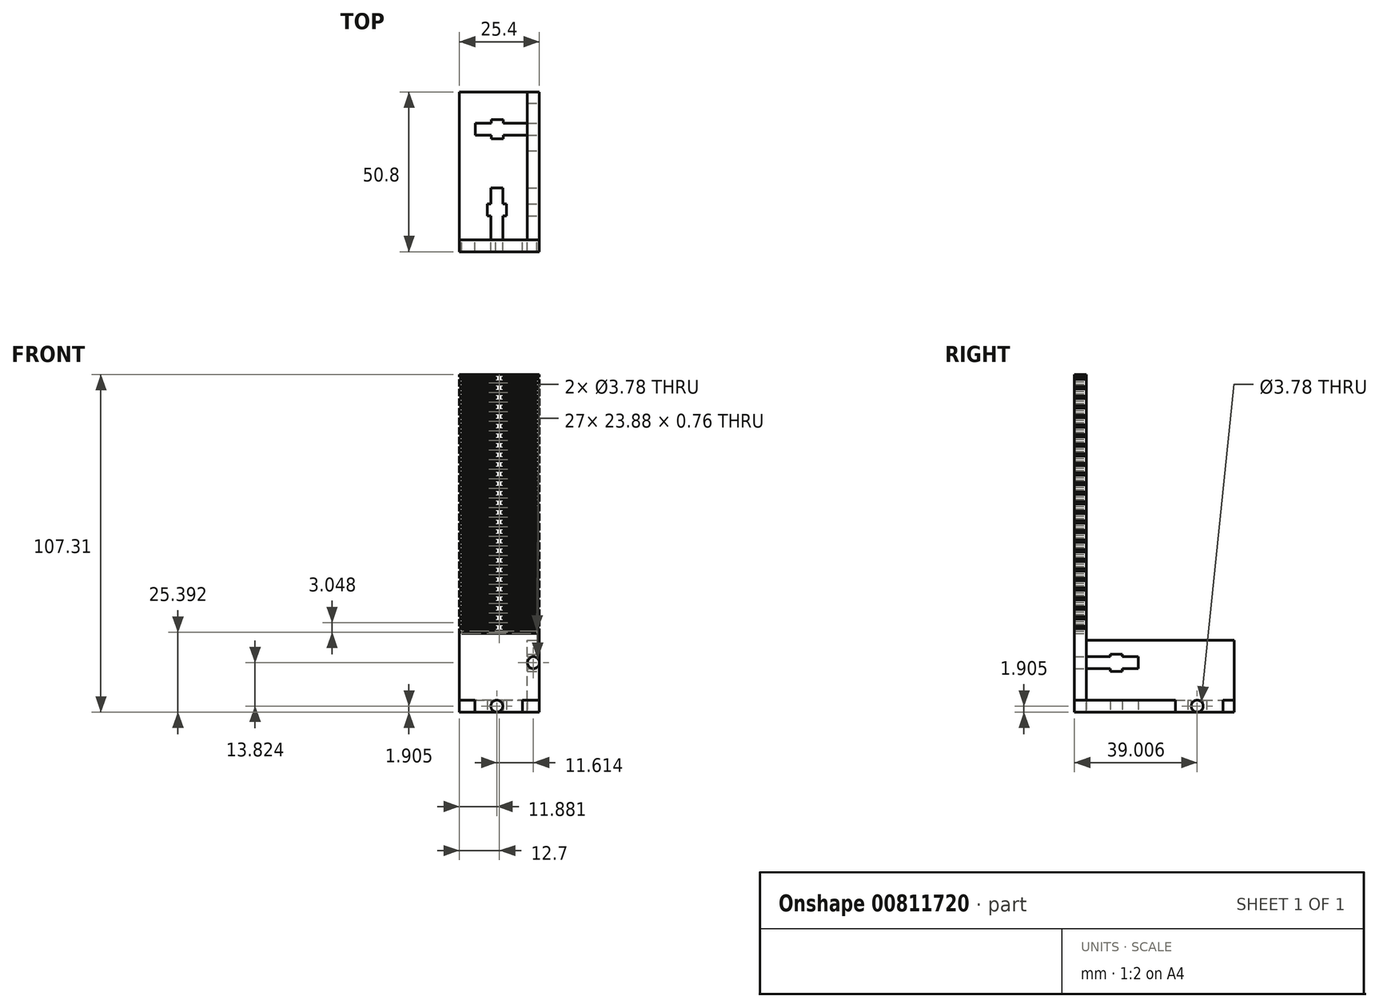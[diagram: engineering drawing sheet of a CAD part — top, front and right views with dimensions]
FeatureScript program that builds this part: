
annotation { "Feature Type Name" : "Feature", "Feature Type Description" : "" }
export const myFeature = defineFeature(function(context is Context, id is Id, definition is map)
    precondition{}
    {
        {
            var Q0;
            Q0=qCreatedBy(makeId("Top.planeOp"),FACE);
            var sketch = newSketch(context, id + "F0", { "sketchPlane" : qUnion([Q0])});
            skLineSegment(sketch, "E0.bottom", {"start": v(-25.4, -50.8) * mm, "end": v(-20.43, -50.8) * mm});
            skLineSegment(sketch, "E0.top", {"start": v(-25.4, 0) * mm, "end": v(0, 0) * mm});
            skLineSegment(sketch, "E0.left", {"start": v(-25.4, -50.8) * mm, "end": v(-25.4, 0) * mm});
            skLineSegment(sketch, "E0.right", {"start": v(0, -50.8) * mm, "end": v(0, -18.7) * mm});
            skLineSegment(sketch, "E1.bottom", {"start": v(-3.8, -9.89) * mm, "end": v(-11.43, -9.89) * mm});
            skLineSegment(sketch, "E1.top", {"start": v(-3.8, -13.7) * mm, "end": v(-11.43, -13.7) * mm});
            skLineSegment(sketch, "E1.right", {"start": v(-20.32, -9.89) * mm, "end": v(-20.32, -13.7) * mm});
            skLineSegment(sketch, "E2.bottom", {"start": v(-15.24, -14.83) * mm, "end": v(-11.43, -14.83) * mm});
            skLineSegment(sketch, "E2.top", {"start": v(-15.24, -8.76) * mm, "end": v(-11.43, -8.76) * mm});
            skLineSegment(sketch, "E2.left", {"start": v(-15.24, -14.83) * mm, "end": v(-15.24, -13.7) * mm});
            skLineSegment(sketch, "E2.right", {"start": v(-11.43, -14.83) * mm, "end": v(-11.43, -13.7) * mm});
            skLineSegment(sketch, "E3.trimOffspring", {"start": v(-11.43, -9.89) * mm, "end": v(-11.43, -8.76) * mm});
            skLineSegment(sketch, "E4.trimOffspring", {"start": v(-15.24, -9.89) * mm, "end": v(-15.24, -8.76) * mm});
            skLineSegment(sketch, "E5.trimOffspring", {"start": v(-15.24, -9.89) * mm, "end": v(-20.32, -9.89) * mm});
            skLineSegment(sketch, "E6.trimOffspring", {"start": v(-15.24, -13.7) * mm, "end": v(-20.32, -13.7) * mm});
            skLineSegment(sketch, "E7.bottom", {"start": v(0, -18.7) * mm, "end": v(-3.8, -18.7) * mm});
            skLineSegment(sketch, "E7.top", {"start": v(0, -3.62) * mm, "end": v(-3.8, -3.62) * mm});
            skLineSegment(sketch, "E7.right", {"start": v(-3.8, -18.7) * mm, "end": v(-3.8, -13.7) * mm});
            skLineSegment(sketch, "E8.trimOffspring", {"start": v(-3.8, -9.89) * mm, "end": v(-3.8, -3.62) * mm});
            skLineSegment(sketch, "E9.trimOffspring", {"start": v(0, -3.62) * mm, "end": v(0, 0) * mm});
            skLineSegment(sketch, "E10.bottom", {"start": v(-11.63, -46.99) * mm, "end": v(-11.63, -39.37) * mm});
            skLineSegment(sketch, "E10.top", {"start": v(-15.44, -46.99) * mm, "end": v(-15.44, -39.37) * mm});
            skLineSegment(sketch, "E10.right", {"start": v(-11.63, -30.48) * mm, "end": v(-15.44, -30.48) * mm});
            skLineSegment(sketch, "E11.bottom", {"start": v(-16.57, -35.56) * mm, "end": v(-16.57, -39.37) * mm});
            skLineSegment(sketch, "E11.top", {"start": v(-10.5, -35.56) * mm, "end": v(-10.5, -39.37) * mm});
            skLineSegment(sketch, "E11.left", {"start": v(-16.57, -35.56) * mm, "end": v(-15.44, -35.56) * mm});
            skLineSegment(sketch, "E11.right", {"start": v(-16.57, -39.37) * mm, "end": v(-15.44, -39.37) * mm});
            skLineSegment(sketch, "E12.trimOffspring", {"start": v(-11.63, -39.37) * mm, "end": v(-10.5, -39.37) * mm});
            skLineSegment(sketch, "E13.trimOffspring", {"start": v(-11.63, -35.56) * mm, "end": v(-10.5, -35.56) * mm});
            skLineSegment(sketch, "E14.trimOffspring", {"start": v(-11.63, -35.56) * mm, "end": v(-11.63, -30.48) * mm});
            skLineSegment(sketch, "E15.trimOffspring", {"start": v(-15.44, -35.56) * mm, "end": v(-15.44, -30.48) * mm});
            skLineSegment(sketch, "E16.bottom", {"start": v(-20.43, -50.8) * mm, "end": v(-20.43, -46.99) * mm});
            skLineSegment(sketch, "E16.top", {"start": v(-5.36, -50.8) * mm, "end": v(-5.36, -46.99) * mm});
            skLineSegment(sketch, "E16.right", {"start": v(-20.43, -46.99) * mm, "end": v(-15.44, -46.99) * mm});
            skLineSegment(sketch, "E17.trimOffspring", {"start": v(-11.63, -46.99) * mm, "end": v(-5.36, -46.99) * mm});
            skLineSegment(sketch, "E18.trimOffspring", {"start": v(-5.36, -50.8) * mm, "end": v(0, -50.8) * mm});
            skSolve(sketch);
        }
        {
            var Q0;
            Q0=makeQuery(id+"F0.imprint","IMPRINT",FACE,{"disambiguationData":[TD([[makeQuery(id+"F0.imprint","IMPRINT",EDGE,{"derivedFrom":sQuery(id+"F0.wireOp",EDGE,"E0.bottom")}),1.0]])]});
            extrude(context, id + "F1", {"entities" : qUnion([Q0]), "depth" : 3.8 * mm});
        }
        {
            var Q0;
            Q0=makeQuery(id+"F1.opExtrude","SWEPT_FACE",FACE,{"disambiguationData":[OSD([sQuery(id+"F0.wireOp",EDGE,"E16.right")])]});
            var sketch = newSketch(context, id + "F2", { "sketchPlane" : qUnion([Q0])});
            skLineSegment(sketch, "E19.bottom", {"start": v(-5.36, 0) * mm, "end": v(-20.43, 0) * mm});
            skLineSegment(sketch, "E20", {"start": v(-20.43, 0) * mm, "end": v(-20.43, 3.81) * mm});
            skLineSegment(sketch, "E21", {"start": v(-20.43, 3.81) * mm, "end": v(-25.4, 3.81) * mm});
            skLineSegment(sketch, "E22.MirrorCS", {"start": v(-5.36, 0) * mm, "end": v(-5.36, 3.81) * mm});
            skLineSegment(sketch, "E23.MirrorCS", {"start": v(-5.36, 3.81) * mm, "end": v(0, 3.81) * mm});
            skCircle(sketch, "E24", {"center": v(-13.52, 1.9) * mm, "radius": 1.9 * mm});
            skLineSegment(sketch, "E25", {"start": v(-20.43, 1.9) * mm, "end": v(-5.36, 1.9) * mm, "construction": true});
            skLineSegment(sketch, "E26", {"start": v(-25.4, 107.3) * mm, "end": v(-12.7, 107.3) * mm});
            skLineSegment(sketch, "E27", {"start": v(-12.7, 107.3) * mm, "end": v(-12.7, -12.92) * mm, "construction": true});
            skLineSegment(sketch, "E28.bottom", {"start": v(-25.4, 106.55) * mm, "end": v(-13.82, 106.55) * mm});
            skLineSegment(sketch, "E28.top", {"start": v(-25.4, 105.78) * mm, "end": v(-13.82, 105.78) * mm});
            skLineSegment(sketch, "E28.right", {"start": v(-13.82, 106.55) * mm, "end": v(-13.82, 105.78) * mm});
            skLineSegment(sketch, "E29.trimOffspring", {"start": v(-25.4, 106.55) * mm, "end": v(-25.4, 107.3) * mm});
            skPoint(sketch, "E30.start.orphan", {"position": v(0, 107.3) * mm});
            skLineSegment(sketch, "E31.MirrorCS", {"start": v(-11.58, 106.55) * mm, "end": v(-11.58, 105.78) * mm});
            skLineSegment(sketch, "E32.MirrorCS", {"start": v(0, 107.3) * mm, "end": v(-12.7, 107.3) * mm});
            skLineSegment(sketch, "E33.MirrorCS", {"start": v(0, 105.78) * mm, "end": v(-11.58, 105.78) * mm});
            skLineSegment(sketch, "E34.MirrorCS", {"start": v(0, 106.55) * mm, "end": v(0, 107.3) * mm});
            skLineSegment(sketch, "E35.MirrorCS", {"start": v(0, 106.55) * mm, "end": v(-11.58, 106.55) * mm});
            skLineSegment(sketch, "E36.bottom", {"start": v(-24.64, 105.02) * mm, "end": v(-0.76, 105.02) * mm});
            skLineSegment(sketch, "E36.top", {"start": v(-24.64, 104.26) * mm, "end": v(-0.76, 104.26) * mm});
            skLineSegment(sketch, "E36.left", {"start": v(-24.64, 105.02) * mm, "end": v(-24.64, 104.26) * mm});
            skLineSegment(sketch, "E36.right", {"start": v(-0.76, 105.02) * mm, "end": v(-0.76, 104.26) * mm});
            skLineSegment(sketch, "E37", {"start": v(-25.4, 105.78) * mm, "end": v(-25.4, 104.26) * mm});
            skLineSegment(sketch, "E38.MirrorCS", {"start": v(-38.1, 107.3) * mm, "end": v(-38.1, -12.92) * mm, "construction": true});
            skLineSegment(sketch, "E39.MirrorCS", {"start": v(0, 105.78) * mm, "end": v(0, 104.26) * mm});
            skLineSegment(sketch, "E40.0.1.0", {"start": v(-0.76, 101.97) * mm, "end": v(-0.76, 101.21) * mm});
            skLineSegment(sketch, "E40.0.1.1", {"start": v(0, 103.5) * mm, "end": v(0, 104.26) * mm});
            skPoint(sketch, "E40.0.1.2", {"position": v(0, 104.26) * mm});
            skLineSegment(sketch, "E40.0.1.3", {"start": v(-24.64, 101.97) * mm, "end": v(-24.64, 101.21) * mm});
            skLineSegment(sketch, "E40.0.1.4", {"start": v(0, 103.5) * mm, "end": v(-11.58, 103.5) * mm});
            skLineSegment(sketch, "E40.0.1.5", {"start": v(-25.4, 103.5) * mm, "end": v(-13.82, 103.5) * mm});
            skLineSegment(sketch, "E40.0.1.6", {"start": v(0, 102.74) * mm, "end": v(-11.58, 102.74) * mm});
            skLineSegment(sketch, "E40.0.1.7", {"start": v(0, 102.74) * mm, "end": v(0, 101.21) * mm});
            skLineSegment(sketch, "E40.0.1.8", {"start": v(-25.4, 102.74) * mm, "end": v(-25.4, 101.21) * mm});
            skLineSegment(sketch, "E40.0.1.9", {"start": v(-24.64, 101.21) * mm, "end": v(-0.76, 101.21) * mm});
            skLineSegment(sketch, "E40.0.1.10", {"start": v(-25.4, 103.5) * mm, "end": v(-25.4, 104.26) * mm});
            skLineSegment(sketch, "E40.0.1.11", {"start": v(-13.82, 103.5) * mm, "end": v(-13.82, 102.74) * mm});
            skLineSegment(sketch, "E40.0.1.12", {"start": v(-11.58, 103.5) * mm, "end": v(-11.58, 102.74) * mm});
            skLineSegment(sketch, "E40.0.1.13", {"start": v(-24.64, 101.97) * mm, "end": v(-0.76, 101.97) * mm});
            skLineSegment(sketch, "E40.0.1.14", {"start": v(-25.4, 102.74) * mm, "end": v(-13.82, 102.74) * mm});
            skLineSegment(sketch, "E40.0.2.0", {"start": v(-0.76, 98.93) * mm, "end": v(-0.76, 98.16) * mm});
            skLineSegment(sketch, "E40.0.2.1", {"start": v(0, 100.45) * mm, "end": v(0, 101.21) * mm});
            skPoint(sketch, "E40.0.2.2", {"position": v(0, 101.21) * mm});
            skLineSegment(sketch, "E40.0.2.3", {"start": v(-24.64, 98.93) * mm, "end": v(-24.64, 98.16) * mm});
            skLineSegment(sketch, "E40.0.2.4", {"start": v(0, 100.45) * mm, "end": v(-11.58, 100.45) * mm});
            skLineSegment(sketch, "E40.0.2.5", {"start": v(-25.4, 100.45) * mm, "end": v(-13.82, 100.45) * mm});
            skLineSegment(sketch, "E40.0.2.6", {"start": v(0, 99.69) * mm, "end": v(-11.58, 99.69) * mm});
            skLineSegment(sketch, "E40.0.2.7", {"start": v(0, 99.69) * mm, "end": v(0, 98.16) * mm});
            skLineSegment(sketch, "E40.0.2.8", {"start": v(-25.4, 99.69) * mm, "end": v(-25.4, 98.16) * mm});
            skLineSegment(sketch, "E40.0.2.9", {"start": v(-24.64, 98.16) * mm, "end": v(-0.76, 98.16) * mm});
            skLineSegment(sketch, "E40.0.2.10", {"start": v(-25.4, 100.45) * mm, "end": v(-25.4, 101.21) * mm});
            skLineSegment(sketch, "E40.0.2.11", {"start": v(-13.82, 100.45) * mm, "end": v(-13.82, 99.69) * mm});
            skLineSegment(sketch, "E40.0.2.12", {"start": v(-11.58, 100.45) * mm, "end": v(-11.58, 99.69) * mm});
            skLineSegment(sketch, "E40.0.2.13", {"start": v(-24.64, 98.93) * mm, "end": v(-0.76, 98.93) * mm});
            skLineSegment(sketch, "E40.0.2.14", {"start": v(-25.4, 99.69) * mm, "end": v(-13.82, 99.69) * mm});
            skLineSegment(sketch, "E40.0.3.0", {"start": v(-0.76, 95.88) * mm, "end": v(-0.76, 95.12) * mm});
            skLineSegment(sketch, "E40.0.3.1", {"start": v(0, 97.4) * mm, "end": v(0, 98.16) * mm});
            skPoint(sketch, "E40.0.3.2", {"position": v(0, 98.16) * mm});
            skLineSegment(sketch, "E40.0.3.3", {"start": v(-24.64, 95.88) * mm, "end": v(-24.64, 95.12) * mm});
            skLineSegment(sketch, "E40.0.3.4", {"start": v(0, 97.4) * mm, "end": v(-11.58, 97.4) * mm});
            skLineSegment(sketch, "E40.0.3.5", {"start": v(-25.4, 97.4) * mm, "end": v(-13.82, 97.4) * mm});
            skLineSegment(sketch, "E40.0.3.6", {"start": v(0, 96.64) * mm, "end": v(-11.58, 96.64) * mm});
            skLineSegment(sketch, "E40.0.3.7", {"start": v(0, 96.64) * mm, "end": v(0, 95.12) * mm});
            skLineSegment(sketch, "E40.0.3.8", {"start": v(-25.4, 96.64) * mm, "end": v(-25.4, 95.12) * mm});
            skLineSegment(sketch, "E40.0.3.9", {"start": v(-24.64, 95.12) * mm, "end": v(-0.76, 95.12) * mm});
            skLineSegment(sketch, "E40.0.3.10", {"start": v(-25.4, 97.4) * mm, "end": v(-25.4, 98.16) * mm});
            skLineSegment(sketch, "E40.0.3.11", {"start": v(-13.82, 97.4) * mm, "end": v(-13.82, 96.64) * mm});
            skLineSegment(sketch, "E40.0.3.12", {"start": v(-11.58, 97.4) * mm, "end": v(-11.58, 96.64) * mm});
            skLineSegment(sketch, "E40.0.3.13", {"start": v(-24.64, 95.88) * mm, "end": v(-0.76, 95.88) * mm});
            skLineSegment(sketch, "E40.0.3.14", {"start": v(-25.4, 96.64) * mm, "end": v(-13.82, 96.64) * mm});
            skLineSegment(sketch, "E40.0.4.0", {"start": v(-0.76, 92.83) * mm, "end": v(-0.76, 92.07) * mm});
            skLineSegment(sketch, "E40.0.4.1", {"start": v(0, 94.35) * mm, "end": v(0, 95.12) * mm});
            skPoint(sketch, "E40.0.4.2", {"position": v(0, 95.12) * mm});
            skLineSegment(sketch, "E40.0.4.3", {"start": v(-24.64, 92.83) * mm, "end": v(-24.64, 92.07) * mm});
            skLineSegment(sketch, "E40.0.4.4", {"start": v(0, 94.35) * mm, "end": v(-11.58, 94.35) * mm});
            skLineSegment(sketch, "E40.0.4.5", {"start": v(-25.4, 94.35) * mm, "end": v(-13.82, 94.35) * mm});
            skLineSegment(sketch, "E40.0.4.6", {"start": v(0, 93.6) * mm, "end": v(-11.58, 93.6) * mm});
            skLineSegment(sketch, "E40.0.4.7", {"start": v(0, 93.6) * mm, "end": v(0, 92.07) * mm});
            skLineSegment(sketch, "E40.0.4.8", {"start": v(-25.4, 93.6) * mm, "end": v(-25.4, 92.07) * mm});
            skLineSegment(sketch, "E40.0.4.9", {"start": v(-24.64, 92.07) * mm, "end": v(-0.76, 92.07) * mm});
            skLineSegment(sketch, "E40.0.4.10", {"start": v(-25.4, 94.35) * mm, "end": v(-25.4, 95.12) * mm});
            skLineSegment(sketch, "E40.0.4.11", {"start": v(-13.82, 94.35) * mm, "end": v(-13.82, 93.6) * mm});
            skLineSegment(sketch, "E40.0.4.12", {"start": v(-11.58, 94.35) * mm, "end": v(-11.58, 93.6) * mm});
            skLineSegment(sketch, "E40.0.4.13", {"start": v(-24.64, 92.83) * mm, "end": v(-0.76, 92.83) * mm});
            skLineSegment(sketch, "E40.0.4.14", {"start": v(-25.4, 93.6) * mm, "end": v(-13.82, 93.6) * mm});
            skLineSegment(sketch, "E40.0.5.0", {"start": v(-0.76, 89.78) * mm, "end": v(-0.76, 89.02) * mm});
            skLineSegment(sketch, "E40.0.5.1", {"start": v(0, 91.3) * mm, "end": v(0, 92.07) * mm});
            skPoint(sketch, "E40.0.5.2", {"position": v(0, 92.07) * mm});
            skLineSegment(sketch, "E40.0.5.3", {"start": v(-24.64, 89.78) * mm, "end": v(-24.64, 89.02) * mm});
            skLineSegment(sketch, "E40.0.5.4", {"start": v(0, 91.3) * mm, "end": v(-11.58, 91.3) * mm});
            skLineSegment(sketch, "E40.0.5.5", {"start": v(-25.4, 91.3) * mm, "end": v(-13.82, 91.3) * mm});
            skLineSegment(sketch, "E40.0.5.6", {"start": v(0, 90.54) * mm, "end": v(-11.58, 90.54) * mm});
            skLineSegment(sketch, "E40.0.5.7", {"start": v(0, 90.54) * mm, "end": v(0, 89.02) * mm});
            skLineSegment(sketch, "E40.0.5.8", {"start": v(-25.4, 90.54) * mm, "end": v(-25.4, 89.02) * mm});
            skLineSegment(sketch, "E40.0.5.9", {"start": v(-24.64, 89.02) * mm, "end": v(-0.76, 89.02) * mm});
            skLineSegment(sketch, "E40.0.5.10", {"start": v(-25.4, 91.3) * mm, "end": v(-25.4, 92.07) * mm});
            skLineSegment(sketch, "E40.0.5.11", {"start": v(-13.82, 91.3) * mm, "end": v(-13.82, 90.54) * mm});
            skLineSegment(sketch, "E40.0.5.12", {"start": v(-11.58, 91.3) * mm, "end": v(-11.58, 90.54) * mm});
            skLineSegment(sketch, "E40.0.5.13", {"start": v(-24.64, 89.78) * mm, "end": v(-0.76, 89.78) * mm});
            skLineSegment(sketch, "E40.0.5.14", {"start": v(-25.4, 90.54) * mm, "end": v(-13.82, 90.54) * mm});
            skLineSegment(sketch, "E40.0.6.0", {"start": v(-0.76, 86.73) * mm, "end": v(-0.76, 85.97) * mm});
            skLineSegment(sketch, "E40.0.6.1", {"start": v(0, 88.26) * mm, "end": v(0, 89.02) * mm});
            skPoint(sketch, "E40.0.6.2", {"position": v(0, 89.02) * mm});
            skLineSegment(sketch, "E40.0.6.3", {"start": v(-24.64, 86.73) * mm, "end": v(-24.64, 85.97) * mm});
            skLineSegment(sketch, "E40.0.6.4", {"start": v(0, 88.26) * mm, "end": v(-11.58, 88.26) * mm});
            skLineSegment(sketch, "E40.0.6.5", {"start": v(-25.4, 88.26) * mm, "end": v(-13.82, 88.26) * mm});
            skLineSegment(sketch, "E40.0.6.6", {"start": v(0, 87.5) * mm, "end": v(-11.58, 87.5) * mm});
            skLineSegment(sketch, "E40.0.6.7", {"start": v(0, 87.5) * mm, "end": v(0, 85.97) * mm});
            skLineSegment(sketch, "E40.0.6.8", {"start": v(-25.4, 87.5) * mm, "end": v(-25.4, 85.97) * mm});
            skLineSegment(sketch, "E40.0.6.9", {"start": v(-24.64, 85.97) * mm, "end": v(-0.76, 85.97) * mm});
            skLineSegment(sketch, "E40.0.6.10", {"start": v(-25.4, 88.26) * mm, "end": v(-25.4, 89.02) * mm});
            skLineSegment(sketch, "E40.0.6.11", {"start": v(-13.82, 88.26) * mm, "end": v(-13.82, 87.5) * mm});
            skLineSegment(sketch, "E40.0.6.12", {"start": v(-11.58, 88.26) * mm, "end": v(-11.58, 87.5) * mm});
            skLineSegment(sketch, "E40.0.6.13", {"start": v(-24.64, 86.73) * mm, "end": v(-0.76, 86.73) * mm});
            skLineSegment(sketch, "E40.0.6.14", {"start": v(-25.4, 87.5) * mm, "end": v(-13.82, 87.5) * mm});
            skLineSegment(sketch, "E40.0.7.0", {"start": v(-0.76, 83.69) * mm, "end": v(-0.76, 82.92) * mm});
            skLineSegment(sketch, "E40.0.7.1", {"start": v(0, 85.2) * mm, "end": v(0, 85.97) * mm});
            skPoint(sketch, "E40.0.7.2", {"position": v(0, 85.97) * mm});
            skLineSegment(sketch, "E40.0.7.3", {"start": v(-24.64, 83.69) * mm, "end": v(-24.64, 82.92) * mm});
            skLineSegment(sketch, "E40.0.7.4", {"start": v(0, 85.2) * mm, "end": v(-11.58, 85.2) * mm});
            skLineSegment(sketch, "E40.0.7.5", {"start": v(-25.4, 85.2) * mm, "end": v(-13.82, 85.2) * mm});
            skLineSegment(sketch, "E40.0.7.6", {"start": v(0, 84.45) * mm, "end": v(-11.58, 84.45) * mm});
            skLineSegment(sketch, "E40.0.7.7", {"start": v(0, 84.45) * mm, "end": v(0, 82.92) * mm});
            skLineSegment(sketch, "E40.0.7.8", {"start": v(-25.4, 84.45) * mm, "end": v(-25.4, 82.92) * mm});
            skLineSegment(sketch, "E40.0.7.9", {"start": v(-24.64, 82.92) * mm, "end": v(-0.76, 82.92) * mm});
            skLineSegment(sketch, "E40.0.7.10", {"start": v(-25.4, 85.2) * mm, "end": v(-25.4, 85.97) * mm});
            skLineSegment(sketch, "E40.0.7.11", {"start": v(-13.82, 85.2) * mm, "end": v(-13.82, 84.45) * mm});
            skLineSegment(sketch, "E40.0.7.12", {"start": v(-11.58, 85.2) * mm, "end": v(-11.58, 84.45) * mm});
            skLineSegment(sketch, "E40.0.7.13", {"start": v(-24.64, 83.69) * mm, "end": v(-0.76, 83.69) * mm});
            skLineSegment(sketch, "E40.0.7.14", {"start": v(-25.4, 84.45) * mm, "end": v(-13.82, 84.45) * mm});
            skLineSegment(sketch, "E40.0.8.0", {"start": v(-0.76, 80.64) * mm, "end": v(-0.76, 79.88) * mm});
            skLineSegment(sketch, "E40.0.8.1", {"start": v(0, 82.16) * mm, "end": v(0, 82.92) * mm});
            skPoint(sketch, "E40.0.8.2", {"position": v(0, 82.92) * mm});
            skLineSegment(sketch, "E40.0.8.3", {"start": v(-24.64, 80.64) * mm, "end": v(-24.64, 79.88) * mm});
            skLineSegment(sketch, "E40.0.8.4", {"start": v(0, 82.16) * mm, "end": v(-11.58, 82.16) * mm});
            skLineSegment(sketch, "E40.0.8.5", {"start": v(-25.4, 82.16) * mm, "end": v(-13.82, 82.16) * mm});
            skLineSegment(sketch, "E40.0.8.6", {"start": v(0, 81.4) * mm, "end": v(-11.58, 81.4) * mm});
            skLineSegment(sketch, "E40.0.8.7", {"start": v(0, 81.4) * mm, "end": v(0, 79.88) * mm});
            skLineSegment(sketch, "E40.0.8.8", {"start": v(-25.4, 81.4) * mm, "end": v(-25.4, 79.88) * mm});
            skLineSegment(sketch, "E40.0.8.9", {"start": v(-24.64, 79.88) * mm, "end": v(-0.76, 79.88) * mm});
            skLineSegment(sketch, "E40.0.8.10", {"start": v(-25.4, 82.16) * mm, "end": v(-25.4, 82.92) * mm});
            skLineSegment(sketch, "E40.0.8.11", {"start": v(-13.82, 82.16) * mm, "end": v(-13.82, 81.4) * mm});
            skLineSegment(sketch, "E40.0.8.12", {"start": v(-11.58, 82.16) * mm, "end": v(-11.58, 81.4) * mm});
            skLineSegment(sketch, "E40.0.8.13", {"start": v(-24.64, 80.64) * mm, "end": v(-0.76, 80.64) * mm});
            skLineSegment(sketch, "E40.0.8.14", {"start": v(-25.4, 81.4) * mm, "end": v(-13.82, 81.4) * mm});
            skLineSegment(sketch, "E40.0.9.0", {"start": v(-0.76, 77.59) * mm, "end": v(-0.76, 76.83) * mm});
            skLineSegment(sketch, "E40.0.9.1", {"start": v(0, 79.11) * mm, "end": v(0, 79.88) * mm});
            skPoint(sketch, "E40.0.9.2", {"position": v(0, 79.88) * mm});
            skLineSegment(sketch, "E40.0.9.3", {"start": v(-24.64, 77.59) * mm, "end": v(-24.64, 76.83) * mm});
            skLineSegment(sketch, "E40.0.9.4", {"start": v(0, 79.11) * mm, "end": v(-11.58, 79.11) * mm});
            skLineSegment(sketch, "E40.0.9.5", {"start": v(-25.4, 79.11) * mm, "end": v(-13.82, 79.11) * mm});
            skLineSegment(sketch, "E40.0.9.6", {"start": v(0, 78.35) * mm, "end": v(-11.58, 78.35) * mm});
            skLineSegment(sketch, "E40.0.9.7", {"start": v(0, 78.35) * mm, "end": v(0, 76.83) * mm});
            skLineSegment(sketch, "E40.0.9.8", {"start": v(-25.4, 78.35) * mm, "end": v(-25.4, 76.83) * mm});
            skLineSegment(sketch, "E40.0.9.9", {"start": v(-24.64, 76.83) * mm, "end": v(-0.76, 76.83) * mm});
            skLineSegment(sketch, "E40.0.9.10", {"start": v(-25.4, 79.11) * mm, "end": v(-25.4, 79.88) * mm});
            skLineSegment(sketch, "E40.0.9.11", {"start": v(-13.82, 79.11) * mm, "end": v(-13.82, 78.35) * mm});
            skLineSegment(sketch, "E40.0.9.12", {"start": v(-11.58, 79.11) * mm, "end": v(-11.58, 78.35) * mm});
            skLineSegment(sketch, "E40.0.9.13", {"start": v(-24.64, 77.59) * mm, "end": v(-0.76, 77.59) * mm});
            skLineSegment(sketch, "E40.0.9.14", {"start": v(-25.4, 78.35) * mm, "end": v(-13.82, 78.35) * mm});
            skLineSegment(sketch, "E40.0.10.0", {"start": v(-0.76, 74.54) * mm, "end": v(-0.76, 73.78) * mm});
            skLineSegment(sketch, "E40.0.10.1", {"start": v(0, 76.07) * mm, "end": v(0, 76.83) * mm});
            skPoint(sketch, "E40.0.10.2", {"position": v(0, 76.83) * mm});
            skLineSegment(sketch, "E40.0.10.3", {"start": v(-24.64, 74.54) * mm, "end": v(-24.64, 73.78) * mm});
            skLineSegment(sketch, "E40.0.10.4", {"start": v(0, 76.07) * mm, "end": v(-11.58, 76.07) * mm});
            skLineSegment(sketch, "E40.0.10.5", {"start": v(-25.4, 76.07) * mm, "end": v(-13.82, 76.07) * mm});
            skLineSegment(sketch, "E40.0.10.6", {"start": v(0, 75.3) * mm, "end": v(-11.58, 75.3) * mm});
            skLineSegment(sketch, "E40.0.10.7", {"start": v(0, 75.3) * mm, "end": v(0, 73.78) * mm});
            skLineSegment(sketch, "E40.0.10.8", {"start": v(-25.4, 75.3) * mm, "end": v(-25.4, 73.78) * mm});
            skLineSegment(sketch, "E40.0.10.9", {"start": v(-24.64, 73.78) * mm, "end": v(-0.76, 73.78) * mm});
            skLineSegment(sketch, "E40.0.10.10", {"start": v(-25.4, 76.07) * mm, "end": v(-25.4, 76.83) * mm});
            skLineSegment(sketch, "E40.0.10.11", {"start": v(-13.82, 76.07) * mm, "end": v(-13.82, 75.3) * mm});
            skLineSegment(sketch, "E40.0.10.12", {"start": v(-11.58, 76.07) * mm, "end": v(-11.58, 75.3) * mm});
            skLineSegment(sketch, "E40.0.10.13", {"start": v(-24.64, 74.54) * mm, "end": v(-0.76, 74.54) * mm});
            skLineSegment(sketch, "E40.0.10.14", {"start": v(-25.4, 75.3) * mm, "end": v(-13.82, 75.3) * mm});
            skLineSegment(sketch, "E40.0.11.0", {"start": v(-0.76, 71.5) * mm, "end": v(-0.76, 70.73) * mm});
            skLineSegment(sketch, "E40.0.11.1", {"start": v(0, 73.02) * mm, "end": v(0, 73.78) * mm});
            skPoint(sketch, "E40.0.11.2", {"position": v(0, 73.78) * mm});
            skLineSegment(sketch, "E40.0.11.3", {"start": v(-24.64, 71.5) * mm, "end": v(-24.64, 70.73) * mm});
            skLineSegment(sketch, "E40.0.11.4", {"start": v(0, 73.02) * mm, "end": v(-11.58, 73.02) * mm});
            skLineSegment(sketch, "E40.0.11.5", {"start": v(-25.4, 73.02) * mm, "end": v(-13.82, 73.02) * mm});
            skLineSegment(sketch, "E40.0.11.6", {"start": v(0, 72.26) * mm, "end": v(-11.58, 72.26) * mm});
            skLineSegment(sketch, "E40.0.11.7", {"start": v(0, 72.26) * mm, "end": v(0, 70.73) * mm});
            skLineSegment(sketch, "E40.0.11.8", {"start": v(-25.4, 72.26) * mm, "end": v(-25.4, 70.73) * mm});
            skLineSegment(sketch, "E40.0.11.9", {"start": v(-24.64, 70.73) * mm, "end": v(-0.76, 70.73) * mm});
            skLineSegment(sketch, "E40.0.11.10", {"start": v(-25.4, 73.02) * mm, "end": v(-25.4, 73.78) * mm});
            skLineSegment(sketch, "E40.0.11.11", {"start": v(-13.82, 73.02) * mm, "end": v(-13.82, 72.26) * mm});
            skLineSegment(sketch, "E40.0.11.12", {"start": v(-11.58, 73.02) * mm, "end": v(-11.58, 72.26) * mm});
            skLineSegment(sketch, "E40.0.11.13", {"start": v(-24.64, 71.5) * mm, "end": v(-0.76, 71.5) * mm});
            skLineSegment(sketch, "E40.0.11.14", {"start": v(-25.4, 72.26) * mm, "end": v(-13.82, 72.26) * mm});
            skLineSegment(sketch, "E40.0.12.0", {"start": v(-0.76, 68.45) * mm, "end": v(-0.76, 67.68) * mm});
            skLineSegment(sketch, "E40.0.12.1", {"start": v(0, 69.97) * mm, "end": v(0, 70.73) * mm});
            skPoint(sketch, "E40.0.12.2", {"position": v(0, 70.73) * mm});
            skLineSegment(sketch, "E40.0.12.3", {"start": v(-24.64, 68.45) * mm, "end": v(-24.64, 67.68) * mm});
            skLineSegment(sketch, "E40.0.12.4", {"start": v(0, 69.97) * mm, "end": v(-11.58, 69.97) * mm});
            skLineSegment(sketch, "E40.0.12.5", {"start": v(-25.4, 69.97) * mm, "end": v(-13.82, 69.97) * mm});
            skLineSegment(sketch, "E40.0.12.6", {"start": v(0, 69.2) * mm, "end": v(-11.58, 69.2) * mm});
            skLineSegment(sketch, "E40.0.12.7", {"start": v(0, 69.2) * mm, "end": v(0, 67.68) * mm});
            skLineSegment(sketch, "E40.0.12.8", {"start": v(-25.4, 69.2) * mm, "end": v(-25.4, 67.68) * mm});
            skLineSegment(sketch, "E40.0.12.9", {"start": v(-24.64, 67.68) * mm, "end": v(-0.76, 67.68) * mm});
            skLineSegment(sketch, "E40.0.12.10", {"start": v(-25.4, 69.97) * mm, "end": v(-25.4, 70.73) * mm});
            skLineSegment(sketch, "E40.0.12.11", {"start": v(-13.82, 69.97) * mm, "end": v(-13.82, 69.2) * mm});
            skLineSegment(sketch, "E40.0.12.12", {"start": v(-11.58, 69.97) * mm, "end": v(-11.58, 69.2) * mm});
            skLineSegment(sketch, "E40.0.12.13", {"start": v(-24.64, 68.45) * mm, "end": v(-0.76, 68.45) * mm});
            skLineSegment(sketch, "E40.0.12.14", {"start": v(-25.4, 69.2) * mm, "end": v(-13.82, 69.2) * mm});
            skLineSegment(sketch, "E40.0.13.0", {"start": v(-0.76, 65.4) * mm, "end": v(-0.76, 64.64) * mm});
            skLineSegment(sketch, "E40.0.13.1", {"start": v(0, 66.92) * mm, "end": v(0, 67.68) * mm});
            skPoint(sketch, "E40.0.13.2", {"position": v(0, 67.68) * mm});
            skLineSegment(sketch, "E40.0.13.3", {"start": v(-24.64, 65.4) * mm, "end": v(-24.64, 64.64) * mm});
            skLineSegment(sketch, "E40.0.13.4", {"start": v(0, 66.92) * mm, "end": v(-11.58, 66.92) * mm});
            skLineSegment(sketch, "E40.0.13.5", {"start": v(-25.4, 66.92) * mm, "end": v(-13.82, 66.92) * mm});
            skLineSegment(sketch, "E40.0.13.6", {"start": v(0, 66.16) * mm, "end": v(-11.58, 66.16) * mm});
            skLineSegment(sketch, "E40.0.13.7", {"start": v(0, 66.16) * mm, "end": v(0, 64.64) * mm});
            skLineSegment(sketch, "E40.0.13.8", {"start": v(-25.4, 66.16) * mm, "end": v(-25.4, 64.64) * mm});
            skLineSegment(sketch, "E40.0.13.9", {"start": v(-24.64, 64.64) * mm, "end": v(-0.76, 64.64) * mm});
            skLineSegment(sketch, "E40.0.13.10", {"start": v(-25.4, 66.92) * mm, "end": v(-25.4, 67.68) * mm});
            skLineSegment(sketch, "E40.0.13.11", {"start": v(-13.82, 66.92) * mm, "end": v(-13.82, 66.16) * mm});
            skLineSegment(sketch, "E40.0.13.12", {"start": v(-11.58, 66.92) * mm, "end": v(-11.58, 66.16) * mm});
            skLineSegment(sketch, "E40.0.13.13", {"start": v(-24.64, 65.4) * mm, "end": v(-0.76, 65.4) * mm});
            skLineSegment(sketch, "E40.0.13.14", {"start": v(-25.4, 66.16) * mm, "end": v(-13.82, 66.16) * mm});
            skLineSegment(sketch, "E40.0.14.0", {"start": v(-0.76, 62.35) * mm, "end": v(-0.76, 61.59) * mm});
            skLineSegment(sketch, "E40.0.14.1", {"start": v(0, 63.87) * mm, "end": v(0, 64.64) * mm});
            skPoint(sketch, "E40.0.14.2", {"position": v(0, 64.64) * mm});
            skLineSegment(sketch, "E40.0.14.3", {"start": v(-24.64, 62.35) * mm, "end": v(-24.64, 61.59) * mm});
            skLineSegment(sketch, "E40.0.14.4", {"start": v(0, 63.87) * mm, "end": v(-11.58, 63.87) * mm});
            skLineSegment(sketch, "E40.0.14.5", {"start": v(-25.4, 63.87) * mm, "end": v(-13.82, 63.87) * mm});
            skLineSegment(sketch, "E40.0.14.6", {"start": v(0, 63.11) * mm, "end": v(-11.58, 63.11) * mm});
            skLineSegment(sketch, "E40.0.14.7", {"start": v(0, 63.11) * mm, "end": v(0, 61.59) * mm});
            skLineSegment(sketch, "E40.0.14.8", {"start": v(-25.4, 63.11) * mm, "end": v(-25.4, 61.59) * mm});
            skLineSegment(sketch, "E40.0.14.9", {"start": v(-24.64, 61.59) * mm, "end": v(-0.76, 61.59) * mm});
            skLineSegment(sketch, "E40.0.14.10", {"start": v(-25.4, 63.87) * mm, "end": v(-25.4, 64.64) * mm});
            skLineSegment(sketch, "E40.0.14.11", {"start": v(-13.82, 63.87) * mm, "end": v(-13.82, 63.11) * mm});
            skLineSegment(sketch, "E40.0.14.12", {"start": v(-11.58, 63.87) * mm, "end": v(-11.58, 63.11) * mm});
            skLineSegment(sketch, "E40.0.14.13", {"start": v(-24.64, 62.35) * mm, "end": v(-0.76, 62.35) * mm});
            skLineSegment(sketch, "E40.0.14.14", {"start": v(-25.4, 63.11) * mm, "end": v(-13.82, 63.11) * mm});
            skLineSegment(sketch, "E40.0.15.0", {"start": v(-0.76, 59.3) * mm, "end": v(-0.76, 58.54) * mm});
            skLineSegment(sketch, "E40.0.15.1", {"start": v(0, 60.83) * mm, "end": v(0, 61.59) * mm});
            skPoint(sketch, "E40.0.15.2", {"position": v(0, 61.59) * mm});
            skLineSegment(sketch, "E40.0.15.3", {"start": v(-24.64, 59.3) * mm, "end": v(-24.64, 58.54) * mm});
            skLineSegment(sketch, "E40.0.15.4", {"start": v(0, 60.83) * mm, "end": v(-11.58, 60.83) * mm});
            skLineSegment(sketch, "E40.0.15.5", {"start": v(-25.4, 60.83) * mm, "end": v(-13.82, 60.83) * mm});
            skLineSegment(sketch, "E40.0.15.6", {"start": v(0, 60.06) * mm, "end": v(-11.58, 60.06) * mm});
            skLineSegment(sketch, "E40.0.15.7", {"start": v(0, 60.06) * mm, "end": v(0, 58.54) * mm});
            skLineSegment(sketch, "E40.0.15.8", {"start": v(-25.4, 60.06) * mm, "end": v(-25.4, 58.54) * mm});
            skLineSegment(sketch, "E40.0.15.9", {"start": v(-24.64, 58.54) * mm, "end": v(-0.76, 58.54) * mm});
            skLineSegment(sketch, "E40.0.15.10", {"start": v(-25.4, 60.83) * mm, "end": v(-25.4, 61.59) * mm});
            skLineSegment(sketch, "E40.0.15.11", {"start": v(-13.82, 60.83) * mm, "end": v(-13.82, 60.06) * mm});
            skLineSegment(sketch, "E40.0.15.12", {"start": v(-11.58, 60.83) * mm, "end": v(-11.58, 60.06) * mm});
            skLineSegment(sketch, "E40.0.15.13", {"start": v(-24.64, 59.3) * mm, "end": v(-0.76, 59.3) * mm});
            skLineSegment(sketch, "E40.0.15.14", {"start": v(-25.4, 60.06) * mm, "end": v(-13.82, 60.06) * mm});
            skLineSegment(sketch, "E40.0.16.0", {"start": v(-0.76, 56.25) * mm, "end": v(-0.76, 55.5) * mm});
            skLineSegment(sketch, "E40.0.16.1", {"start": v(0, 57.78) * mm, "end": v(0, 58.54) * mm});
            skPoint(sketch, "E40.0.16.2", {"position": v(0, 58.54) * mm});
            skLineSegment(sketch, "E40.0.16.3", {"start": v(-24.64, 56.25) * mm, "end": v(-24.64, 55.5) * mm});
            skLineSegment(sketch, "E40.0.16.4", {"start": v(0, 57.78) * mm, "end": v(-11.58, 57.78) * mm});
            skLineSegment(sketch, "E40.0.16.5", {"start": v(-25.4, 57.78) * mm, "end": v(-13.82, 57.78) * mm});
            skLineSegment(sketch, "E40.0.16.6", {"start": v(0, 57.02) * mm, "end": v(-11.58, 57.02) * mm});
            skLineSegment(sketch, "E40.0.16.7", {"start": v(0, 57.02) * mm, "end": v(0, 55.5) * mm});
            skLineSegment(sketch, "E40.0.16.8", {"start": v(-25.4, 57.02) * mm, "end": v(-25.4, 55.5) * mm});
            skLineSegment(sketch, "E40.0.16.9", {"start": v(-24.64, 55.5) * mm, "end": v(-0.76, 55.5) * mm});
            skLineSegment(sketch, "E40.0.16.10", {"start": v(-25.4, 57.78) * mm, "end": v(-25.4, 58.54) * mm});
            skLineSegment(sketch, "E40.0.16.11", {"start": v(-13.82, 57.78) * mm, "end": v(-13.82, 57.02) * mm});
            skLineSegment(sketch, "E40.0.16.12", {"start": v(-11.58, 57.78) * mm, "end": v(-11.58, 57.02) * mm});
            skLineSegment(sketch, "E40.0.16.13", {"start": v(-24.64, 56.25) * mm, "end": v(-0.76, 56.25) * mm});
            skLineSegment(sketch, "E40.0.16.14", {"start": v(-25.4, 57.02) * mm, "end": v(-13.82, 57.02) * mm});
            skLineSegment(sketch, "E40.0.17.0", {"start": v(-0.76, 53.2) * mm, "end": v(-0.76, 52.44) * mm});
            skLineSegment(sketch, "E40.0.17.1", {"start": v(0, 54.73) * mm, "end": v(0, 55.5) * mm});
            skPoint(sketch, "E40.0.17.2", {"position": v(0, 55.5) * mm});
            skLineSegment(sketch, "E40.0.17.3", {"start": v(-24.64, 53.2) * mm, "end": v(-24.64, 52.44) * mm});
            skLineSegment(sketch, "E40.0.17.4", {"start": v(0, 54.73) * mm, "end": v(-11.58, 54.73) * mm});
            skLineSegment(sketch, "E40.0.17.5", {"start": v(-25.4, 54.73) * mm, "end": v(-13.82, 54.73) * mm});
            skLineSegment(sketch, "E40.0.17.6", {"start": v(0, 53.97) * mm, "end": v(-11.58, 53.97) * mm});
            skLineSegment(sketch, "E40.0.17.7", {"start": v(0, 53.97) * mm, "end": v(0, 52.44) * mm});
            skLineSegment(sketch, "E40.0.17.8", {"start": v(-25.4, 53.97) * mm, "end": v(-25.4, 52.44) * mm});
            skLineSegment(sketch, "E40.0.17.9", {"start": v(-24.64, 52.44) * mm, "end": v(-0.76, 52.44) * mm});
            skLineSegment(sketch, "E40.0.17.10", {"start": v(-25.4, 54.73) * mm, "end": v(-25.4, 55.5) * mm});
            skLineSegment(sketch, "E40.0.17.11", {"start": v(-13.82, 54.73) * mm, "end": v(-13.82, 53.97) * mm});
            skLineSegment(sketch, "E40.0.17.12", {"start": v(-11.58, 54.73) * mm, "end": v(-11.58, 53.97) * mm});
            skLineSegment(sketch, "E40.0.17.13", {"start": v(-24.64, 53.2) * mm, "end": v(-0.76, 53.2) * mm});
            skLineSegment(sketch, "E40.0.17.14", {"start": v(-25.4, 53.97) * mm, "end": v(-13.82, 53.97) * mm});
            skLineSegment(sketch, "E40.0.18.0", {"start": v(-0.76, 50.16) * mm, "end": v(-0.76, 49.4) * mm});
            skLineSegment(sketch, "E40.0.18.1", {"start": v(0, 51.68) * mm, "end": v(0, 52.44) * mm});
            skPoint(sketch, "E40.0.18.2", {"position": v(0, 52.44) * mm});
            skLineSegment(sketch, "E40.0.18.3", {"start": v(-24.64, 50.16) * mm, "end": v(-24.64, 49.4) * mm});
            skLineSegment(sketch, "E40.0.18.4", {"start": v(0, 51.68) * mm, "end": v(-11.58, 51.68) * mm});
            skLineSegment(sketch, "E40.0.18.5", {"start": v(-25.4, 51.68) * mm, "end": v(-13.82, 51.68) * mm});
            skLineSegment(sketch, "E40.0.18.6", {"start": v(0, 50.92) * mm, "end": v(-11.58, 50.92) * mm});
            skLineSegment(sketch, "E40.0.18.7", {"start": v(0, 50.92) * mm, "end": v(0, 49.4) * mm});
            skLineSegment(sketch, "E40.0.18.8", {"start": v(-25.4, 50.92) * mm, "end": v(-25.4, 49.4) * mm});
            skLineSegment(sketch, "E40.0.18.9", {"start": v(-24.64, 49.4) * mm, "end": v(-0.76, 49.4) * mm});
            skLineSegment(sketch, "E40.0.18.10", {"start": v(-25.4, 51.68) * mm, "end": v(-25.4, 52.44) * mm});
            skLineSegment(sketch, "E40.0.18.11", {"start": v(-13.82, 51.68) * mm, "end": v(-13.82, 50.92) * mm});
            skLineSegment(sketch, "E40.0.18.12", {"start": v(-11.58, 51.68) * mm, "end": v(-11.58, 50.92) * mm});
            skLineSegment(sketch, "E40.0.18.13", {"start": v(-24.64, 50.16) * mm, "end": v(-0.76, 50.16) * mm});
            skLineSegment(sketch, "E40.0.18.14", {"start": v(-25.4, 50.92) * mm, "end": v(-13.82, 50.92) * mm});
            skLineSegment(sketch, "E40.0.19.0", {"start": v(-0.76, 47.1) * mm, "end": v(-0.76, 46.35) * mm});
            skLineSegment(sketch, "E40.0.19.1", {"start": v(0, 48.63) * mm, "end": v(0, 49.4) * mm});
            skPoint(sketch, "E40.0.19.2", {"position": v(0, 49.4) * mm});
            skLineSegment(sketch, "E40.0.19.3", {"start": v(-24.64, 47.1) * mm, "end": v(-24.64, 46.35) * mm});
            skLineSegment(sketch, "E40.0.19.4", {"start": v(0, 48.63) * mm, "end": v(-11.58, 48.63) * mm});
            skLineSegment(sketch, "E40.0.19.5", {"start": v(-25.4, 48.63) * mm, "end": v(-13.82, 48.63) * mm});
            skLineSegment(sketch, "E40.0.19.6", {"start": v(0, 47.87) * mm, "end": v(-11.58, 47.87) * mm});
            skLineSegment(sketch, "E40.0.19.7", {"start": v(0, 47.87) * mm, "end": v(0, 46.35) * mm});
            skLineSegment(sketch, "E40.0.19.8", {"start": v(-25.4, 47.87) * mm, "end": v(-25.4, 46.35) * mm});
            skLineSegment(sketch, "E40.0.19.9", {"start": v(-24.64, 46.35) * mm, "end": v(-0.76, 46.35) * mm});
            skLineSegment(sketch, "E40.0.19.10", {"start": v(-25.4, 48.63) * mm, "end": v(-25.4, 49.4) * mm});
            skLineSegment(sketch, "E40.0.19.11", {"start": v(-13.82, 48.63) * mm, "end": v(-13.82, 47.87) * mm});
            skLineSegment(sketch, "E40.0.19.12", {"start": v(-11.58, 48.63) * mm, "end": v(-11.58, 47.87) * mm});
            skLineSegment(sketch, "E40.0.19.13", {"start": v(-24.64, 47.1) * mm, "end": v(-0.76, 47.1) * mm});
            skLineSegment(sketch, "E40.0.19.14", {"start": v(-25.4, 47.87) * mm, "end": v(-13.82, 47.87) * mm});
            skLineSegment(sketch, "E40.0.20.0", {"start": v(-0.76, 44.06) * mm, "end": v(-0.76, 43.3) * mm});
            skLineSegment(sketch, "E40.0.20.1", {"start": v(0, 45.59) * mm, "end": v(0, 46.35) * mm});
            skPoint(sketch, "E40.0.20.2", {"position": v(0, 46.35) * mm});
            skLineSegment(sketch, "E40.0.20.3", {"start": v(-24.64, 44.06) * mm, "end": v(-24.64, 43.3) * mm});
            skLineSegment(sketch, "E40.0.20.4", {"start": v(0, 45.59) * mm, "end": v(-11.58, 45.59) * mm});
            skLineSegment(sketch, "E40.0.20.5", {"start": v(-25.4, 45.59) * mm, "end": v(-13.82, 45.59) * mm});
            skLineSegment(sketch, "E40.0.20.6", {"start": v(0, 44.82) * mm, "end": v(-11.58, 44.82) * mm});
            skLineSegment(sketch, "E40.0.20.7", {"start": v(0, 44.82) * mm, "end": v(0, 43.3) * mm});
            skLineSegment(sketch, "E40.0.20.8", {"start": v(-25.4, 44.82) * mm, "end": v(-25.4, 43.3) * mm});
            skLineSegment(sketch, "E40.0.20.9", {"start": v(-24.64, 43.3) * mm, "end": v(-0.76, 43.3) * mm});
            skLineSegment(sketch, "E40.0.20.10", {"start": v(-25.4, 45.59) * mm, "end": v(-25.4, 46.35) * mm});
            skLineSegment(sketch, "E40.0.20.11", {"start": v(-13.82, 45.59) * mm, "end": v(-13.82, 44.82) * mm});
            skLineSegment(sketch, "E40.0.20.12", {"start": v(-11.58, 45.59) * mm, "end": v(-11.58, 44.82) * mm});
            skLineSegment(sketch, "E40.0.20.13", {"start": v(-24.64, 44.06) * mm, "end": v(-0.76, 44.06) * mm});
            skLineSegment(sketch, "E40.0.20.14", {"start": v(-25.4, 44.82) * mm, "end": v(-13.82, 44.82) * mm});
            skLineSegment(sketch, "E40.0.21.0", {"start": v(-0.76, 41.01) * mm, "end": v(-0.76, 40.25) * mm});
            skLineSegment(sketch, "E40.0.21.1", {"start": v(0, 42.54) * mm, "end": v(0, 43.3) * mm});
            skPoint(sketch, "E40.0.21.2", {"position": v(0, 43.3) * mm});
            skLineSegment(sketch, "E40.0.21.3", {"start": v(-24.64, 41.01) * mm, "end": v(-24.64, 40.25) * mm});
            skLineSegment(sketch, "E40.0.21.4", {"start": v(0, 42.54) * mm, "end": v(-11.58, 42.54) * mm});
            skLineSegment(sketch, "E40.0.21.5", {"start": v(-25.4, 42.54) * mm, "end": v(-13.82, 42.54) * mm});
            skLineSegment(sketch, "E40.0.21.6", {"start": v(0, 41.78) * mm, "end": v(-11.58, 41.78) * mm});
            skLineSegment(sketch, "E40.0.21.7", {"start": v(0, 41.78) * mm, "end": v(0, 40.25) * mm});
            skLineSegment(sketch, "E40.0.21.8", {"start": v(-25.4, 41.78) * mm, "end": v(-25.4, 40.25) * mm});
            skLineSegment(sketch, "E40.0.21.9", {"start": v(-24.64, 40.25) * mm, "end": v(-0.76, 40.25) * mm});
            skLineSegment(sketch, "E40.0.21.10", {"start": v(-25.4, 42.54) * mm, "end": v(-25.4, 43.3) * mm});
            skLineSegment(sketch, "E40.0.21.11", {"start": v(-13.82, 42.54) * mm, "end": v(-13.82, 41.78) * mm});
            skLineSegment(sketch, "E40.0.21.12", {"start": v(-11.58, 42.54) * mm, "end": v(-11.58, 41.78) * mm});
            skLineSegment(sketch, "E40.0.21.13", {"start": v(-24.64, 41.01) * mm, "end": v(-0.76, 41.01) * mm});
            skLineSegment(sketch, "E40.0.21.14", {"start": v(-25.4, 41.78) * mm, "end": v(-13.82, 41.78) * mm});
            skLineSegment(sketch, "E40.0.22.0", {"start": v(-0.76, 37.97) * mm, "end": v(-0.76, 37.2) * mm});
            skLineSegment(sketch, "E40.0.22.1", {"start": v(0, 39.49) * mm, "end": v(0, 40.25) * mm});
            skPoint(sketch, "E40.0.22.2", {"position": v(0, 40.25) * mm});
            skLineSegment(sketch, "E40.0.22.3", {"start": v(-24.64, 37.97) * mm, "end": v(-24.64, 37.2) * mm});
            skLineSegment(sketch, "E40.0.22.4", {"start": v(0, 39.49) * mm, "end": v(-11.58, 39.49) * mm});
            skLineSegment(sketch, "E40.0.22.5", {"start": v(-25.4, 39.49) * mm, "end": v(-13.82, 39.49) * mm});
            skLineSegment(sketch, "E40.0.22.6", {"start": v(0, 38.73) * mm, "end": v(-11.58, 38.73) * mm});
            skLineSegment(sketch, "E40.0.22.7", {"start": v(0, 38.73) * mm, "end": v(0, 37.2) * mm});
            skLineSegment(sketch, "E40.0.22.8", {"start": v(-25.4, 38.73) * mm, "end": v(-25.4, 37.2) * mm});
            skLineSegment(sketch, "E40.0.22.9", {"start": v(-24.64, 37.2) * mm, "end": v(-0.76, 37.2) * mm});
            skLineSegment(sketch, "E40.0.22.10", {"start": v(-25.4, 39.49) * mm, "end": v(-25.4, 40.25) * mm});
            skLineSegment(sketch, "E40.0.22.11", {"start": v(-13.82, 39.49) * mm, "end": v(-13.82, 38.73) * mm});
            skLineSegment(sketch, "E40.0.22.12", {"start": v(-11.58, 39.49) * mm, "end": v(-11.58, 38.73) * mm});
            skLineSegment(sketch, "E40.0.22.13", {"start": v(-24.64, 37.97) * mm, "end": v(-0.76, 37.97) * mm});
            skLineSegment(sketch, "E40.0.22.14", {"start": v(-25.4, 38.73) * mm, "end": v(-13.82, 38.73) * mm});
            skLineSegment(sketch, "E40.0.23.0", {"start": v(-0.76, 34.92) * mm, "end": v(-0.76, 34.16) * mm});
            skLineSegment(sketch, "E40.0.23.1", {"start": v(0, 36.44) * mm, "end": v(0, 37.2) * mm});
            skPoint(sketch, "E40.0.23.2", {"position": v(0, 37.2) * mm});
            skLineSegment(sketch, "E40.0.23.3", {"start": v(-24.64, 34.92) * mm, "end": v(-24.64, 34.16) * mm});
            skLineSegment(sketch, "E40.0.23.4", {"start": v(0, 36.44) * mm, "end": v(-11.58, 36.44) * mm});
            skLineSegment(sketch, "E40.0.23.5", {"start": v(-25.4, 36.44) * mm, "end": v(-13.82, 36.44) * mm});
            skLineSegment(sketch, "E40.0.23.6", {"start": v(0, 35.68) * mm, "end": v(-11.58, 35.68) * mm});
            skLineSegment(sketch, "E40.0.23.7", {"start": v(0, 35.68) * mm, "end": v(0, 34.16) * mm});
            skLineSegment(sketch, "E40.0.23.8", {"start": v(-25.4, 35.68) * mm, "end": v(-25.4, 34.16) * mm});
            skLineSegment(sketch, "E40.0.23.9", {"start": v(-24.64, 34.16) * mm, "end": v(-0.76, 34.16) * mm});
            skLineSegment(sketch, "E40.0.23.10", {"start": v(-25.4, 36.44) * mm, "end": v(-25.4, 37.2) * mm});
            skLineSegment(sketch, "E40.0.23.11", {"start": v(-13.82, 36.44) * mm, "end": v(-13.82, 35.68) * mm});
            skLineSegment(sketch, "E40.0.23.12", {"start": v(-11.58, 36.44) * mm, "end": v(-11.58, 35.68) * mm});
            skLineSegment(sketch, "E40.0.23.13", {"start": v(-24.64, 34.92) * mm, "end": v(-0.76, 34.92) * mm});
            skLineSegment(sketch, "E40.0.23.14", {"start": v(-25.4, 35.68) * mm, "end": v(-13.82, 35.68) * mm});
            skLineSegment(sketch, "E40.0.24.0", {"start": v(-0.76, 31.87) * mm, "end": v(-0.76, 31.1) * mm});
            skLineSegment(sketch, "E40.0.24.1", {"start": v(0, 33.4) * mm, "end": v(0, 34.16) * mm});
            skPoint(sketch, "E40.0.24.2", {"position": v(0, 34.16) * mm});
            skLineSegment(sketch, "E40.0.24.3", {"start": v(-24.64, 31.87) * mm, "end": v(-24.64, 31.1) * mm});
            skLineSegment(sketch, "E40.0.24.4", {"start": v(0, 33.4) * mm, "end": v(-11.58, 33.4) * mm});
            skLineSegment(sketch, "E40.0.24.5", {"start": v(-25.4, 33.4) * mm, "end": v(-13.82, 33.4) * mm});
            skLineSegment(sketch, "E40.0.24.6", {"start": v(0, 32.63) * mm, "end": v(-11.58, 32.63) * mm});
            skLineSegment(sketch, "E40.0.24.7", {"start": v(0, 32.63) * mm, "end": v(0, 31.1) * mm});
            skLineSegment(sketch, "E40.0.24.8", {"start": v(-25.4, 32.63) * mm, "end": v(-25.4, 31.1) * mm});
            skLineSegment(sketch, "E40.0.24.9", {"start": v(-24.64, 31.1) * mm, "end": v(-0.76, 31.1) * mm});
            skLineSegment(sketch, "E40.0.24.10", {"start": v(-25.4, 33.4) * mm, "end": v(-25.4, 34.16) * mm});
            skLineSegment(sketch, "E40.0.24.11", {"start": v(-13.82, 33.4) * mm, "end": v(-13.82, 32.63) * mm});
            skLineSegment(sketch, "E40.0.24.12", {"start": v(-11.58, 33.4) * mm, "end": v(-11.58, 32.63) * mm});
            skLineSegment(sketch, "E40.0.24.13", {"start": v(-24.64, 31.87) * mm, "end": v(-0.76, 31.87) * mm});
            skLineSegment(sketch, "E40.0.24.14", {"start": v(-25.4, 32.63) * mm, "end": v(-13.82, 32.63) * mm});
            skLineSegment(sketch, "E40.direction1", {"start": v(-25.4, 104.26) * mm, "end": v(-45.16, 104.26) * mm, "construction": true});
            skLineSegment(sketch, "E40.direction2", {"start": v(-25.4, 104.26) * mm, "end": v(-25.4, 101.21) * mm, "construction": true});
            skLineSegment(sketch, "E41", {"start": v(0, 3.8) * mm, "end": v(0, 25.01) * mm});
            skLineSegment(sketch, "E42", {"start": v(-25.4, 3.81) * mm, "end": v(-25.4, 25.01) * mm});
            skLineSegment(sketch, "E43.0.0.25", {"start": v(-0.76, 28.82) * mm, "end": v(-0.76, 28.06) * mm});
            skLineSegment(sketch, "E43.3.0.25", {"start": v(0, 30.35) * mm, "end": v(0, 31.1) * mm});
            skPoint(sketch, "E43.6.0.25", {"position": v(0, 31.1) * mm});
            skLineSegment(sketch, "E43.7.0.25", {"start": v(-24.64, 28.82) * mm, "end": v(-24.64, 28.06) * mm});
            skLineSegment(sketch, "E43.10.0.25", {"start": v(0, 30.35) * mm, "end": v(-11.58, 30.35) * mm});
            skLineSegment(sketch, "E43.13.0.25", {"start": v(-25.4, 30.35) * mm, "end": v(-13.82, 30.35) * mm});
            skLineSegment(sketch, "E43.16.0.25", {"start": v(0, 29.58) * mm, "end": v(-11.58, 29.58) * mm});
            skLineSegment(sketch, "E43.19.0.25", {"start": v(0, 29.58) * mm, "end": v(0, 28.06) * mm});
            skLineSegment(sketch, "E43.22.0.25", {"start": v(-25.4, 29.58) * mm, "end": v(-25.4, 28.06) * mm});
            skLineSegment(sketch, "E43.25.0.25", {"start": v(-24.64, 28.06) * mm, "end": v(-0.76, 28.06) * mm});
            skLineSegment(sketch, "E43.28.0.25", {"start": v(-25.4, 30.35) * mm, "end": v(-25.4, 31.1) * mm});
            skLineSegment(sketch, "E43.31.0.25", {"start": v(-13.82, 30.35) * mm, "end": v(-13.82, 29.58) * mm});
            skLineSegment(sketch, "E43.34.0.25", {"start": v(-11.58, 30.35) * mm, "end": v(-11.58, 29.58) * mm});
            skLineSegment(sketch, "E43.37.0.25", {"start": v(-24.64, 28.82) * mm, "end": v(-0.76, 28.82) * mm});
            skLineSegment(sketch, "E43.40.0.25", {"start": v(-25.4, 29.58) * mm, "end": v(-13.82, 29.58) * mm});
            skLineSegment(sketch, "E43.0.0.26", {"start": v(-0.76, 25.77) * mm, "end": v(-0.76, 25.01) * mm});
            skLineSegment(sketch, "E43.3.0.26", {"start": v(0, 27.3) * mm, "end": v(0, 28.06) * mm});
            skPoint(sketch, "E43.6.0.26", {"position": v(0, 28.06) * mm});
            skLineSegment(sketch, "E43.7.0.26", {"start": v(-24.64, 25.77) * mm, "end": v(-24.64, 25.01) * mm});
            skLineSegment(sketch, "E43.10.0.26", {"start": v(0, 27.3) * mm, "end": v(-11.58, 27.3) * mm});
            skLineSegment(sketch, "E43.13.0.26", {"start": v(-25.4, 27.3) * mm, "end": v(-13.82, 27.3) * mm});
            skLineSegment(sketch, "E43.16.0.26", {"start": v(0, 26.54) * mm, "end": v(-11.58, 26.54) * mm});
            skLineSegment(sketch, "E43.19.0.26", {"start": v(0, 26.54) * mm, "end": v(0, 25.01) * mm});
            skLineSegment(sketch, "E43.22.0.26", {"start": v(-25.4, 26.54) * mm, "end": v(-25.4, 25.01) * mm});
            skLineSegment(sketch, "E43.25.0.26", {"start": v(-24.64, 25.01) * mm, "end": v(-0.76, 25.01) * mm});
            skLineSegment(sketch, "E43.28.0.26", {"start": v(-25.4, 27.3) * mm, "end": v(-25.4, 28.06) * mm});
            skLineSegment(sketch, "E43.31.0.26", {"start": v(-13.82, 27.3) * mm, "end": v(-13.82, 26.54) * mm});
            skLineSegment(sketch, "E43.34.0.26", {"start": v(-11.58, 27.3) * mm, "end": v(-11.58, 26.54) * mm});
            skLineSegment(sketch, "E43.37.0.26", {"start": v(-24.64, 25.77) * mm, "end": v(-0.76, 25.77) * mm});
            skLineSegment(sketch, "E43.40.0.26", {"start": v(-25.4, 26.54) * mm, "end": v(-13.82, 26.54) * mm});
            skPoint(sketch, "E44", {"position": v(-1.9, 15.73) * mm});
            skCircle(sketch, "E45", {"center": v(-1.9, 15.73) * mm, "radius": 1.9 * mm});
            skSolve(sketch);
        }
        {
            var Q0;
            Q0=makeQuery(id+"F2.imprint","IMPRINT",FACE,{"disambiguationData":[TD([[makeQuery(id+"F2.imprint","IMPRINT",EDGE,{"derivedFrom":sQuery(id+"F2.wireOp",EDGE,"E21")}),-1.0]])]});
            var Q1;
            {var subQ3=sQuery(id+"F2.wireOp",EDGE,"E20");Q1=makeQuery(id+"F2.imprint","IMPRINT",FACE,{"disambiguationData":[TD([[makeQuery(id+"F2.imprint","IMPRINT",EDGE,{"derivedFrom":subQ3}),1.0]])]});}
            var Q2;
            Q2=makeQuery(id+"F2.imprint","IMPRINT",FACE,{"disambiguationData":[TD([[makeQuery(id+"F2.imprint","IMPRINT",EDGE,{"derivedFrom":sQuery(id+"F2.wireOp",EDGE,"E24")}),1.0]])]});
            extrude(context, id + "F3", {"entities" : qUnion([Q0, Q1, Q2]), "depth" : 3.8 * mm});
        }
        {
            var Q0;
            Q0=sQuery(id+"F2.wireOp",VERTEX,"E24.center");
            var Q1;
            Q1=makeQuery(id+"F3.opExtrude","SWEPT_BODY",BODY,{"disambiguationData":[OSD([sQuery(id+"F2.wireOp",EDGE,"E19.bottom"),sQuery(id+"F2.wireOp",EDGE,"E19.right"),sQuery(id+"F2.wireOp",EDGE,"E20"),sQuery(id+"F2.wireOp",EDGE,"E21"),sQuery(id+"F2.wireOp",EDGE,"E22.MirrorCS"),sQuery(id+"F2.wireOp",EDGE,"E23.MirrorCS"),sQuery(id+"F2.wireOp",EDGE,"E26"),sQuery(id+"F2.wireOp",EDGE,"E30")])]});
            hole(context, id + "F4", {"style" : HoleStyle.SIMPLE, "endStyle" : HoleEndStyle.THROUGH, "oppositeDirection" : true, "holeDiameter" : 3.78 * mm, "locations" : qUnion([Q0]), "scope" : qUnion([Q1]), "isTappedThrough" : true});
        }
        {
            var Q0;
            Q0=makeQuery(id+"F1.opExtrude","SWEPT_FACE",FACE,{"disambiguationData":[OSD([sQuery(id+"F0.wireOp",EDGE,"E0.right")])]});
            var sketch = newSketch(context, id + "F5", { "sketchPlane" : qUnion([Q0])});
            skLineSegment(sketch, "E46.bottom", {"start": v(0, 3.81) * mm, "end": v(-3.62, 3.81) * mm});
            skLineSegment(sketch, "E46.top", {"start": v(0, 22.86) * mm, "end": v(-46.99, 22.86) * mm});
            skLineSegment(sketch, "E46.left", {"start": v(0, 3.81) * mm, "end": v(0, 22.86) * mm});
            skLineSegment(sketch, "E46.right", {"start": v(-46.99, 3.8) * mm, "end": v(-46.99, 13.82) * mm});
            skLineSegment(sketch, "E47.bottom", {"start": v(-46.99, 13.82) * mm, "end": v(-39.37, 13.82) * mm});
            skLineSegment(sketch, "E47.top", {"start": v(-47, 17.63) * mm, "end": v(-39.37, 17.63) * mm});
            skLineSegment(sketch, "E47.right", {"start": v(-30.48, 13.82) * mm, "end": v(-30.48, 17.63) * mm});
            skLineSegment(sketch, "E48.bottom", {"start": v(-35.56, 18.45) * mm, "end": v(-39.37, 18.45) * mm});
            skLineSegment(sketch, "E48.top", {"start": v(-35.56, 13) * mm, "end": v(-39.37, 13) * mm});
            skLineSegment(sketch, "E48.left", {"start": v(-35.56, 18.45) * mm, "end": v(-35.56, 17.63) * mm});
            skLineSegment(sketch, "E48.right", {"start": v(-39.37, 18.45) * mm, "end": v(-39.37, 17.63) * mm});
            skLineSegment(sketch, "E49.trimOffspring", {"start": v(-39.37, 13.82) * mm, "end": v(-39.37, 13) * mm});
            skLineSegment(sketch, "E50.trimOffspring", {"start": v(-35.56, 13.82) * mm, "end": v(-35.56, 13) * mm});
            skLineSegment(sketch, "E51.trimOffspring", {"start": v(-35.56, 13.82) * mm, "end": v(-30.48, 13.82) * mm});
            skLineSegment(sketch, "E52.trimOffspring", {"start": v(-35.56, 17.63) * mm, "end": v(-30.48, 17.63) * mm});
            skLineSegment(sketch, "E53.bottom", {"start": v(-18.7, 0) * mm, "end": v(-3.62, 0) * mm});
            skLineSegment(sketch, "E53.left", {"start": v(-18.7, 0) * mm, "end": v(-18.7, 3.81) * mm});
            skLineSegment(sketch, "E53.right", {"start": v(-3.62, 0) * mm, "end": v(-3.62, 3.81) * mm});
            skLineSegment(sketch, "E54.trimOffspring", {"start": v(-18.7, 3.8) * mm, "end": v(-46.99, 3.8) * mm});
            skLineSegment(sketch, "E55.trimOffspring", {"start": v(-46.99, 17.63) * mm, "end": v(-46.99, 22.86) * mm});
            skLineSegment(sketch, "E56", {"start": v(-11.8, 0) * mm, "end": v(-11.8, 3.81) * mm, "construction": true});
            skLineSegment(sketch, "E57", {"start": v(-13.7, 1.9) * mm, "end": v(-9.89, 1.9) * mm, "construction": true});
            skPoint(sketch, "E58", {"position": v(-11.8, 1.9) * mm});
            skCircle(sketch, "E59", {"center": v(-11.8, 1.9) * mm, "radius": 1.9 * mm});
            skSolve(sketch);
        }
        {
            var Q0;
            Q0=qSketchRegion(id+"F5",true);
            extrude(context, id + "F6", {"entities" : qUnion([Q0]), "oppositeDirection" : true, "depth" : 3.8 * mm});
        }
        {
            var Q0;
            Q0=sQuery(id+"F5.wireOp",VERTEX,"E58");
            var Q1;
            Q1=makeQuery(id+"F6.opExtrude","SWEPT_BODY",BODY,{"disambiguationData":[OSD([sQuery(id+"F5.wireOp",EDGE,"E46.bottom"),sQuery(id+"F5.wireOp",EDGE,"E46.top"),sQuery(id+"F5.wireOp",EDGE,"E46.left"),sQuery(id+"F5.wireOp",EDGE,"E46.right"),sQuery(id+"F5.wireOp",EDGE,"E47.bottom"),sQuery(id+"F5.wireOp",EDGE,"E47.top"),sQuery(id+"F5.wireOp",EDGE,"E47.right"),sQuery(id+"F5.wireOp",EDGE,"E48.bottom"),sQuery(id+"F5.wireOp",EDGE,"E48.top"),sQuery(id+"F5.wireOp",EDGE,"E48.left"),sQuery(id+"F5.wireOp",EDGE,"E48.right"),sQuery(id+"F5.wireOp",EDGE,"E49.trimOffspring"),sQuery(id+"F5.wireOp",EDGE,"E50.trimOffspring"),sQuery(id+"F5.wireOp",EDGE,"E51.trimOffspring"),sQuery(id+"F5.wireOp",EDGE,"E52.trimOffspring"),sQuery(id+"F5.wireOp",EDGE,"E53.bottom"),sQuery(id+"F5.wireOp",EDGE,"E53.left"),sQuery(id+"F5.wireOp",EDGE,"E53.right"),sQuery(id+"F5.wireOp",EDGE,"E54.trimOffspring"),sQuery(id+"F5.wireOp",EDGE,"E55.trimOffspring")])]});
            hole(context, id + "F7", {"style" : HoleStyle.SIMPLE, "endStyle" : HoleEndStyle.THROUGH, "holeDiameter" : 3.78 * mm, "locations" : qUnion([Q0]), "scope" : qUnion([Q1]), "isTappedThrough" : true});
        }
        {
            var Q0;
            Q0=sQuery(id+"F2.wireOp",VERTEX,"E44");
            var Q1;
            Q1=makeQuery(id+"F3.opExtrude","SWEPT_BODY",BODY,{"disambiguationData":[OSD([sQuery(id+"F2.wireOp",EDGE,"E19.bottom"),sQuery(id+"F2.wireOp",EDGE,"E20"),sQuery(id+"F2.wireOp",EDGE,"E21"),sQuery(id+"F2.wireOp",EDGE,"E22.MirrorCS"),sQuery(id+"F2.wireOp",EDGE,"E23.MirrorCS"),sQuery(id+"F2.wireOp",EDGE,"E26"),sQuery(id+"F2.wireOp",EDGE,"E28.bottom"),sQuery(id+"F2.wireOp",EDGE,"E28.top"),sQuery(id+"F2.wireOp",EDGE,"E28.right"),sQuery(id+"F2.wireOp",EDGE,"E29.trimOffspring"),sQuery(id+"F2.wireOp",EDGE,"E31.MirrorCS"),sQuery(id+"F2.wireOp",EDGE,"E32.MirrorCS"),sQuery(id+"F2.wireOp",EDGE,"E33.MirrorCS"),sQuery(id+"F2.wireOp",EDGE,"E34.MirrorCS"),sQuery(id+"F2.wireOp",EDGE,"E35.MirrorCS"),sQuery(id+"F2.wireOp",EDGE,"E36.bottom"),sQuery(id+"F2.wireOp",EDGE,"E36.top"),sQuery(id+"F2.wireOp",EDGE,"E36.left"),sQuery(id+"F2.wireOp",EDGE,"E36.right"),sQuery(id+"F2.wireOp",EDGE,"E37"),sQuery(id+"F2.wireOp",EDGE,"E39.MirrorCS"),sQuery(id+"F2.wireOp",EDGE,"E40.0.1.0"),sQuery(id+"F2.wireOp",EDGE,"E40.0.1.1"),sQuery(id+"F2.wireOp",EDGE,"E40.0.1.3"),sQuery(id+"F2.wireOp",EDGE,"E40.0.1.4"),sQuery(id+"F2.wireOp",EDGE,"E40.0.1.5"),sQuery(id+"F2.wireOp",EDGE,"E40.0.1.6"),sQuery(id+"F2.wireOp",EDGE,"E40.0.1.7"),sQuery(id+"F2.wireOp",EDGE,"E40.0.1.8"),sQuery(id+"F2.wireOp",EDGE,"E40.0.1.9"),sQuery(id+"F2.wireOp",EDGE,"E40.0.1.10"),sQuery(id+"F2.wireOp",EDGE,"E40.0.1.11"),sQuery(id+"F2.wireOp",EDGE,"E40.0.1.12"),sQuery(id+"F2.wireOp",EDGE,"E40.0.1.13"),sQuery(id+"F2.wireOp",EDGE,"E40.0.1.14"),sQuery(id+"F2.wireOp",EDGE,"E40.0.2.0"),sQuery(id+"F2.wireOp",EDGE,"E40.0.2.1"),sQuery(id+"F2.wireOp",EDGE,"E40.0.2.3"),sQuery(id+"F2.wireOp",EDGE,"E40.0.2.4"),sQuery(id+"F2.wireOp",EDGE,"E40.0.2.5"),sQuery(id+"F2.wireOp",EDGE,"E40.0.2.6"),sQuery(id+"F2.wireOp",EDGE,"E40.0.2.7"),sQuery(id+"F2.wireOp",EDGE,"E40.0.2.8"),sQuery(id+"F2.wireOp",EDGE,"E40.0.2.9"),sQuery(id+"F2.wireOp",EDGE,"E40.0.2.10"),sQuery(id+"F2.wireOp",EDGE,"E40.0.2.11"),sQuery(id+"F2.wireOp",EDGE,"E40.0.2.12"),sQuery(id+"F2.wireOp",EDGE,"E40.0.2.13"),sQuery(id+"F2.wireOp",EDGE,"E40.0.2.14"),sQuery(id+"F2.wireOp",EDGE,"E40.0.3.0"),sQuery(id+"F2.wireOp",EDGE,"E40.0.3.1"),sQuery(id+"F2.wireOp",EDGE,"E40.0.3.3"),sQuery(id+"F2.wireOp",EDGE,"E40.0.3.4"),sQuery(id+"F2.wireOp",EDGE,"E40.0.3.5"),sQuery(id+"F2.wireOp",EDGE,"E40.0.3.6"),sQuery(id+"F2.wireOp",EDGE,"E40.0.3.7"),sQuery(id+"F2.wireOp",EDGE,"E40.0.3.8"),sQuery(id+"F2.wireOp",EDGE,"E40.0.3.9"),sQuery(id+"F2.wireOp",EDGE,"E40.0.3.10"),sQuery(id+"F2.wireOp",EDGE,"E40.0.3.11"),sQuery(id+"F2.wireOp",EDGE,"E40.0.3.12"),sQuery(id+"F2.wireOp",EDGE,"E40.0.3.13"),sQuery(id+"F2.wireOp",EDGE,"E40.0.3.14"),sQuery(id+"F2.wireOp",EDGE,"E40.0.4.0"),sQuery(id+"F2.wireOp",EDGE,"E40.0.4.1"),sQuery(id+"F2.wireOp",EDGE,"E40.0.4.3"),sQuery(id+"F2.wireOp",EDGE,"E40.0.4.4"),sQuery(id+"F2.wireOp",EDGE,"E40.0.4.5"),sQuery(id+"F2.wireOp",EDGE,"E40.0.4.6"),sQuery(id+"F2.wireOp",EDGE,"E40.0.4.7"),sQuery(id+"F2.wireOp",EDGE,"E40.0.4.8"),sQuery(id+"F2.wireOp",EDGE,"E40.0.4.9"),sQuery(id+"F2.wireOp",EDGE,"E40.0.4.10"),sQuery(id+"F2.wireOp",EDGE,"E40.0.4.11"),sQuery(id+"F2.wireOp",EDGE,"E40.0.4.12"),sQuery(id+"F2.wireOp",EDGE,"E40.0.4.13"),sQuery(id+"F2.wireOp",EDGE,"E40.0.4.14"),sQuery(id+"F2.wireOp",EDGE,"E40.0.5.0"),sQuery(id+"F2.wireOp",EDGE,"E40.0.5.1"),sQuery(id+"F2.wireOp",EDGE,"E40.0.5.3"),sQuery(id+"F2.wireOp",EDGE,"E40.0.5.4"),sQuery(id+"F2.wireOp",EDGE,"E40.0.5.5"),sQuery(id+"F2.wireOp",EDGE,"E40.0.5.6"),sQuery(id+"F2.wireOp",EDGE,"E40.0.5.7"),sQuery(id+"F2.wireOp",EDGE,"E40.0.5.8"),sQuery(id+"F2.wireOp",EDGE,"E40.0.5.9"),sQuery(id+"F2.wireOp",EDGE,"E40.0.5.10"),sQuery(id+"F2.wireOp",EDGE,"E40.0.5.11"),sQuery(id+"F2.wireOp",EDGE,"E40.0.5.12"),sQuery(id+"F2.wireOp",EDGE,"E40.0.5.13"),sQuery(id+"F2.wireOp",EDGE,"E40.0.5.14"),sQuery(id+"F2.wireOp",EDGE,"E40.0.6.0"),sQuery(id+"F2.wireOp",EDGE,"E40.0.6.1"),sQuery(id+"F2.wireOp",EDGE,"E40.0.6.3"),sQuery(id+"F2.wireOp",EDGE,"E40.0.6.4"),sQuery(id+"F2.wireOp",EDGE,"E40.0.6.5"),sQuery(id+"F2.wireOp",EDGE,"E40.0.6.6"),sQuery(id+"F2.wireOp",EDGE,"E40.0.6.7"),sQuery(id+"F2.wireOp",EDGE,"E40.0.6.8"),sQuery(id+"F2.wireOp",EDGE,"E40.0.6.9"),sQuery(id+"F2.wireOp",EDGE,"E40.0.6.10"),sQuery(id+"F2.wireOp",EDGE,"E40.0.6.11"),sQuery(id+"F2.wireOp",EDGE,"E40.0.6.12"),sQuery(id+"F2.wireOp",EDGE,"E40.0.6.13"),sQuery(id+"F2.wireOp",EDGE,"E40.0.6.14"),sQuery(id+"F2.wireOp",EDGE,"E40.0.7.0"),sQuery(id+"F2.wireOp",EDGE,"E40.0.7.1"),sQuery(id+"F2.wireOp",EDGE,"E40.0.7.3"),sQuery(id+"F2.wireOp",EDGE,"E40.0.7.4"),sQuery(id+"F2.wireOp",EDGE,"E40.0.7.5"),sQuery(id+"F2.wireOp",EDGE,"E40.0.7.6"),sQuery(id+"F2.wireOp",EDGE,"E40.0.7.7"),sQuery(id+"F2.wireOp",EDGE,"E40.0.7.8"),sQuery(id+"F2.wireOp",EDGE,"E40.0.7.9"),sQuery(id+"F2.wireOp",EDGE,"E40.0.7.10"),sQuery(id+"F2.wireOp",EDGE,"E40.0.7.11"),sQuery(id+"F2.wireOp",EDGE,"E40.0.7.12"),sQuery(id+"F2.wireOp",EDGE,"E40.0.7.13"),sQuery(id+"F2.wireOp",EDGE,"E40.0.7.14"),sQuery(id+"F2.wireOp",EDGE,"E40.0.8.0"),sQuery(id+"F2.wireOp",EDGE,"E40.0.8.1"),sQuery(id+"F2.wireOp",EDGE,"E40.0.8.3"),sQuery(id+"F2.wireOp",EDGE,"E40.0.8.4"),sQuery(id+"F2.wireOp",EDGE,"E40.0.8.5"),sQuery(id+"F2.wireOp",EDGE,"E40.0.8.6"),sQuery(id+"F2.wireOp",EDGE,"E40.0.8.7"),sQuery(id+"F2.wireOp",EDGE,"E40.0.8.8"),sQuery(id+"F2.wireOp",EDGE,"E40.0.8.9"),sQuery(id+"F2.wireOp",EDGE,"E40.0.8.10"),sQuery(id+"F2.wireOp",EDGE,"E40.0.8.11"),sQuery(id+"F2.wireOp",EDGE,"E40.0.8.12"),sQuery(id+"F2.wireOp",EDGE,"E40.0.8.13"),sQuery(id+"F2.wireOp",EDGE,"E40.0.8.14"),sQuery(id+"F2.wireOp",EDGE,"E40.0.9.0"),sQuery(id+"F2.wireOp",EDGE,"E40.0.9.1"),sQuery(id+"F2.wireOp",EDGE,"E40.0.9.3"),sQuery(id+"F2.wireOp",EDGE,"E40.0.9.4"),sQuery(id+"F2.wireOp",EDGE,"E40.0.9.5"),sQuery(id+"F2.wireOp",EDGE,"E40.0.9.6"),sQuery(id+"F2.wireOp",EDGE,"E40.0.9.7"),sQuery(id+"F2.wireOp",EDGE,"E40.0.9.8"),sQuery(id+"F2.wireOp",EDGE,"E40.0.9.9"),sQuery(id+"F2.wireOp",EDGE,"E40.0.9.10"),sQuery(id+"F2.wireOp",EDGE,"E40.0.9.11"),sQuery(id+"F2.wireOp",EDGE,"E40.0.9.12"),sQuery(id+"F2.wireOp",EDGE,"E40.0.9.13"),sQuery(id+"F2.wireOp",EDGE,"E40.0.9.14"),sQuery(id+"F2.wireOp",EDGE,"E40.0.10.0"),sQuery(id+"F2.wireOp",EDGE,"E40.0.10.1"),sQuery(id+"F2.wireOp",EDGE,"E40.0.10.3"),sQuery(id+"F2.wireOp",EDGE,"E40.0.10.4"),sQuery(id+"F2.wireOp",EDGE,"E40.0.10.5"),sQuery(id+"F2.wireOp",EDGE,"E40.0.10.6"),sQuery(id+"F2.wireOp",EDGE,"E40.0.10.7"),sQuery(id+"F2.wireOp",EDGE,"E40.0.10.8"),sQuery(id+"F2.wireOp",EDGE,"E40.0.10.9"),sQuery(id+"F2.wireOp",EDGE,"E40.0.10.10"),sQuery(id+"F2.wireOp",EDGE,"E40.0.10.11"),sQuery(id+"F2.wireOp",EDGE,"E40.0.10.12"),sQuery(id+"F2.wireOp",EDGE,"E40.0.10.13"),sQuery(id+"F2.wireOp",EDGE,"E40.0.10.14"),sQuery(id+"F2.wireOp",EDGE,"E40.0.11.0"),sQuery(id+"F2.wireOp",EDGE,"E40.0.11.1"),sQuery(id+"F2.wireOp",EDGE,"E40.0.11.3"),sQuery(id+"F2.wireOp",EDGE,"E40.0.11.4"),sQuery(id+"F2.wireOp",EDGE,"E40.0.11.5"),sQuery(id+"F2.wireOp",EDGE,"E40.0.11.6"),sQuery(id+"F2.wireOp",EDGE,"E40.0.11.7"),sQuery(id+"F2.wireOp",EDGE,"E40.0.11.8"),sQuery(id+"F2.wireOp",EDGE,"E40.0.11.9"),sQuery(id+"F2.wireOp",EDGE,"E40.0.11.10"),sQuery(id+"F2.wireOp",EDGE,"E40.0.11.11"),sQuery(id+"F2.wireOp",EDGE,"E40.0.11.12"),sQuery(id+"F2.wireOp",EDGE,"E40.0.11.13"),sQuery(id+"F2.wireOp",EDGE,"E40.0.11.14"),sQuery(id+"F2.wireOp",EDGE,"E40.0.12.0"),sQuery(id+"F2.wireOp",EDGE,"E40.0.12.1"),sQuery(id+"F2.wireOp",EDGE,"E40.0.12.3"),sQuery(id+"F2.wireOp",EDGE,"E40.0.12.4"),sQuery(id+"F2.wireOp",EDGE,"E40.0.12.5"),sQuery(id+"F2.wireOp",EDGE,"E40.0.12.6"),sQuery(id+"F2.wireOp",EDGE,"E40.0.12.7"),sQuery(id+"F2.wireOp",EDGE,"E40.0.12.8"),sQuery(id+"F2.wireOp",EDGE,"E40.0.12.9"),sQuery(id+"F2.wireOp",EDGE,"E40.0.12.10"),sQuery(id+"F2.wireOp",EDGE,"E40.0.12.11"),sQuery(id+"F2.wireOp",EDGE,"E40.0.12.12"),sQuery(id+"F2.wireOp",EDGE,"E40.0.12.13"),sQuery(id+"F2.wireOp",EDGE,"E40.0.12.14"),sQuery(id+"F2.wireOp",EDGE,"E40.0.13.0"),sQuery(id+"F2.wireOp",EDGE,"E40.0.13.1"),sQuery(id+"F2.wireOp",EDGE,"E40.0.13.3"),sQuery(id+"F2.wireOp",EDGE,"E40.0.13.4"),sQuery(id+"F2.wireOp",EDGE,"E40.0.13.5"),sQuery(id+"F2.wireOp",EDGE,"E40.0.13.6"),sQuery(id+"F2.wireOp",EDGE,"E40.0.13.7"),sQuery(id+"F2.wireOp",EDGE,"E40.0.13.8"),sQuery(id+"F2.wireOp",EDGE,"E40.0.13.9"),sQuery(id+"F2.wireOp",EDGE,"E40.0.13.10"),sQuery(id+"F2.wireOp",EDGE,"E40.0.13.11"),sQuery(id+"F2.wireOp",EDGE,"E40.0.13.12"),sQuery(id+"F2.wireOp",EDGE,"E40.0.13.13"),sQuery(id+"F2.wireOp",EDGE,"E40.0.13.14"),sQuery(id+"F2.wireOp",EDGE,"E40.0.14.0"),sQuery(id+"F2.wireOp",EDGE,"E40.0.14.1"),sQuery(id+"F2.wireOp",EDGE,"E40.0.14.3"),sQuery(id+"F2.wireOp",EDGE,"E40.0.14.4"),sQuery(id+"F2.wireOp",EDGE,"E40.0.14.5"),sQuery(id+"F2.wireOp",EDGE,"E40.0.14.6"),sQuery(id+"F2.wireOp",EDGE,"E40.0.14.7"),sQuery(id+"F2.wireOp",EDGE,"E40.0.14.8"),sQuery(id+"F2.wireOp",EDGE,"E40.0.14.9"),sQuery(id+"F2.wireOp",EDGE,"E40.0.14.10"),sQuery(id+"F2.wireOp",EDGE,"E40.0.14.11"),sQuery(id+"F2.wireOp",EDGE,"E40.0.14.12"),sQuery(id+"F2.wireOp",EDGE,"E40.0.14.13"),sQuery(id+"F2.wireOp",EDGE,"E40.0.14.14"),sQuery(id+"F2.wireOp",EDGE,"E40.0.15.0"),sQuery(id+"F2.wireOp",EDGE,"E40.0.15.1"),sQuery(id+"F2.wireOp",EDGE,"E40.0.15.3"),sQuery(id+"F2.wireOp",EDGE,"E40.0.15.4"),sQuery(id+"F2.wireOp",EDGE,"E40.0.15.5"),sQuery(id+"F2.wireOp",EDGE,"E40.0.15.6"),sQuery(id+"F2.wireOp",EDGE,"E40.0.15.7"),sQuery(id+"F2.wireOp",EDGE,"E40.0.15.8"),sQuery(id+"F2.wireOp",EDGE,"E40.0.15.9"),sQuery(id+"F2.wireOp",EDGE,"E40.0.15.10"),sQuery(id+"F2.wireOp",EDGE,"E40.0.15.11"),sQuery(id+"F2.wireOp",EDGE,"E40.0.15.12"),sQuery(id+"F2.wireOp",EDGE,"E40.0.15.13"),sQuery(id+"F2.wireOp",EDGE,"E40.0.15.14"),sQuery(id+"F2.wireOp",EDGE,"E40.0.16.0"),sQuery(id+"F2.wireOp",EDGE,"E40.0.16.1"),sQuery(id+"F2.wireOp",EDGE,"E40.0.16.3"),sQuery(id+"F2.wireOp",EDGE,"E40.0.16.4"),sQuery(id+"F2.wireOp",EDGE,"E40.0.16.5"),sQuery(id+"F2.wireOp",EDGE,"E40.0.16.6"),sQuery(id+"F2.wireOp",EDGE,"E40.0.16.7"),sQuery(id+"F2.wireOp",EDGE,"E40.0.16.8"),sQuery(id+"F2.wireOp",EDGE,"E40.0.16.9"),sQuery(id+"F2.wireOp",EDGE,"E40.0.16.10"),sQuery(id+"F2.wireOp",EDGE,"E40.0.16.11"),sQuery(id+"F2.wireOp",EDGE,"E40.0.16.12"),sQuery(id+"F2.wireOp",EDGE,"E40.0.16.13"),sQuery(id+"F2.wireOp",EDGE,"E40.0.16.14"),sQuery(id+"F2.wireOp",EDGE,"E40.0.17.0"),sQuery(id+"F2.wireOp",EDGE,"E40.0.17.1"),sQuery(id+"F2.wireOp",EDGE,"E40.0.17.3"),sQuery(id+"F2.wireOp",EDGE,"E40.0.17.4"),sQuery(id+"F2.wireOp",EDGE,"E40.0.17.5"),sQuery(id+"F2.wireOp",EDGE,"E40.0.17.6"),sQuery(id+"F2.wireOp",EDGE,"E40.0.17.7"),sQuery(id+"F2.wireOp",EDGE,"E40.0.17.8"),sQuery(id+"F2.wireOp",EDGE,"E40.0.17.9"),sQuery(id+"F2.wireOp",EDGE,"E40.0.17.10"),sQuery(id+"F2.wireOp",EDGE,"E40.0.17.11"),sQuery(id+"F2.wireOp",EDGE,"E40.0.17.12"),sQuery(id+"F2.wireOp",EDGE,"E40.0.17.13"),sQuery(id+"F2.wireOp",EDGE,"E40.0.17.14"),sQuery(id+"F2.wireOp",EDGE,"E40.0.18.0"),sQuery(id+"F2.wireOp",EDGE,"E40.0.18.1"),sQuery(id+"F2.wireOp",EDGE,"E40.0.18.3"),sQuery(id+"F2.wireOp",EDGE,"E40.0.18.4"),sQuery(id+"F2.wireOp",EDGE,"E40.0.18.5"),sQuery(id+"F2.wireOp",EDGE,"E40.0.18.6"),sQuery(id+"F2.wireOp",EDGE,"E40.0.18.7"),sQuery(id+"F2.wireOp",EDGE,"E40.0.18.8"),sQuery(id+"F2.wireOp",EDGE,"E40.0.18.9"),sQuery(id+"F2.wireOp",EDGE,"E40.0.18.10"),sQuery(id+"F2.wireOp",EDGE,"E40.0.18.11"),sQuery(id+"F2.wireOp",EDGE,"E40.0.18.12"),sQuery(id+"F2.wireOp",EDGE,"E40.0.18.13"),sQuery(id+"F2.wireOp",EDGE,"E40.0.18.14"),sQuery(id+"F2.wireOp",EDGE,"E40.0.19.0"),sQuery(id+"F2.wireOp",EDGE,"E40.0.19.1"),sQuery(id+"F2.wireOp",EDGE,"E40.0.19.3"),sQuery(id+"F2.wireOp",EDGE,"E40.0.19.4"),sQuery(id+"F2.wireOp",EDGE,"E40.0.19.5"),sQuery(id+"F2.wireOp",EDGE,"E40.0.19.6"),sQuery(id+"F2.wireOp",EDGE,"E40.0.19.7"),sQuery(id+"F2.wireOp",EDGE,"E40.0.19.8"),sQuery(id+"F2.wireOp",EDGE,"E40.0.19.9"),sQuery(id+"F2.wireOp",EDGE,"E40.0.19.10"),sQuery(id+"F2.wireOp",EDGE,"E40.0.19.11"),sQuery(id+"F2.wireOp",EDGE,"E40.0.19.12"),sQuery(id+"F2.wireOp",EDGE,"E40.0.19.13"),sQuery(id+"F2.wireOp",EDGE,"E40.0.19.14"),sQuery(id+"F2.wireOp",EDGE,"E40.0.20.0"),sQuery(id+"F2.wireOp",EDGE,"E40.0.20.1"),sQuery(id+"F2.wireOp",EDGE,"E40.0.20.3"),sQuery(id+"F2.wireOp",EDGE,"E40.0.20.4"),sQuery(id+"F2.wireOp",EDGE,"E40.0.20.5"),sQuery(id+"F2.wireOp",EDGE,"E40.0.20.6"),sQuery(id+"F2.wireOp",EDGE,"E40.0.20.7"),sQuery(id+"F2.wireOp",EDGE,"E40.0.20.8"),sQuery(id+"F2.wireOp",EDGE,"E40.0.20.9"),sQuery(id+"F2.wireOp",EDGE,"E40.0.20.10"),sQuery(id+"F2.wireOp",EDGE,"E40.0.20.11"),sQuery(id+"F2.wireOp",EDGE,"E40.0.20.12"),sQuery(id+"F2.wireOp",EDGE,"E40.0.20.13"),sQuery(id+"F2.wireOp",EDGE,"E40.0.20.14"),sQuery(id+"F2.wireOp",EDGE,"E40.0.21.0"),sQuery(id+"F2.wireOp",EDGE,"E40.0.21.1"),sQuery(id+"F2.wireOp",EDGE,"E40.0.21.3"),sQuery(id+"F2.wireOp",EDGE,"E40.0.21.4"),sQuery(id+"F2.wireOp",EDGE,"E40.0.21.5"),sQuery(id+"F2.wireOp",EDGE,"E40.0.21.6"),sQuery(id+"F2.wireOp",EDGE,"E40.0.21.7"),sQuery(id+"F2.wireOp",EDGE,"E40.0.21.8"),sQuery(id+"F2.wireOp",EDGE,"E40.0.21.9"),sQuery(id+"F2.wireOp",EDGE,"E40.0.21.10"),sQuery(id+"F2.wireOp",EDGE,"E40.0.21.11"),sQuery(id+"F2.wireOp",EDGE,"E40.0.21.12"),sQuery(id+"F2.wireOp",EDGE,"E40.0.21.13"),sQuery(id+"F2.wireOp",EDGE,"E40.0.21.14"),sQuery(id+"F2.wireOp",EDGE,"E40.0.22.0"),sQuery(id+"F2.wireOp",EDGE,"E40.0.22.1"),sQuery(id+"F2.wireOp",EDGE,"E40.0.22.3"),sQuery(id+"F2.wireOp",EDGE,"E40.0.22.4"),sQuery(id+"F2.wireOp",EDGE,"E40.0.22.5"),sQuery(id+"F2.wireOp",EDGE,"E40.0.22.6"),sQuery(id+"F2.wireOp",EDGE,"E40.0.22.7"),sQuery(id+"F2.wireOp",EDGE,"E40.0.22.8"),sQuery(id+"F2.wireOp",EDGE,"E40.0.22.9"),sQuery(id+"F2.wireOp",EDGE,"E40.0.22.10"),sQuery(id+"F2.wireOp",EDGE,"E40.0.22.11"),sQuery(id+"F2.wireOp",EDGE,"E40.0.22.12"),sQuery(id+"F2.wireOp",EDGE,"E40.0.22.13"),sQuery(id+"F2.wireOp",EDGE,"E40.0.22.14"),sQuery(id+"F2.wireOp",EDGE,"E40.0.23.0"),sQuery(id+"F2.wireOp",EDGE,"E40.0.23.1"),sQuery(id+"F2.wireOp",EDGE,"E40.0.23.3"),sQuery(id+"F2.wireOp",EDGE,"E40.0.23.4"),sQuery(id+"F2.wireOp",EDGE,"E40.0.23.5"),sQuery(id+"F2.wireOp",EDGE,"E40.0.23.6"),sQuery(id+"F2.wireOp",EDGE,"E40.0.23.7"),sQuery(id+"F2.wireOp",EDGE,"E40.0.23.8"),sQuery(id+"F2.wireOp",EDGE,"E40.0.23.9"),sQuery(id+"F2.wireOp",EDGE,"E40.0.23.10"),sQuery(id+"F2.wireOp",EDGE,"E40.0.23.11"),sQuery(id+"F2.wireOp",EDGE,"E40.0.23.12"),sQuery(id+"F2.wireOp",EDGE,"E40.0.23.13"),sQuery(id+"F2.wireOp",EDGE,"E40.0.23.14"),sQuery(id+"F2.wireOp",EDGE,"E40.0.24.0"),sQuery(id+"F2.wireOp",EDGE,"E40.0.24.1"),sQuery(id+"F2.wireOp",EDGE,"E40.0.24.3"),sQuery(id+"F2.wireOp",EDGE,"E40.0.24.4"),sQuery(id+"F2.wireOp",EDGE,"E40.0.24.5"),sQuery(id+"F2.wireOp",EDGE,"E40.0.24.6"),sQuery(id+"F2.wireOp",EDGE,"E40.0.24.7"),sQuery(id+"F2.wireOp",EDGE,"E40.0.24.8"),sQuery(id+"F2.wireOp",EDGE,"E40.0.24.9"),sQuery(id+"F2.wireOp",EDGE,"E40.0.24.10"),sQuery(id+"F2.wireOp",EDGE,"E40.0.24.11"),sQuery(id+"F2.wireOp",EDGE,"E40.0.24.12"),sQuery(id+"F2.wireOp",EDGE,"E40.0.24.13"),sQuery(id+"F2.wireOp",EDGE,"E40.0.24.14"),sQuery(id+"F2.wireOp",EDGE,"E41"),sQuery(id+"F2.wireOp",EDGE,"E42"),sQuery(id+"F2.wireOp",EDGE,"E43.0.0.25"),sQuery(id+"F2.wireOp",EDGE,"E43.3.0.25"),sQuery(id+"F2.wireOp",EDGE,"E43.7.0.25"),sQuery(id+"F2.wireOp",EDGE,"E43.10.0.25"),sQuery(id+"F2.wireOp",EDGE,"E43.13.0.25"),sQuery(id+"F2.wireOp",EDGE,"E43.16.0.25"),sQuery(id+"F2.wireOp",EDGE,"E43.19.0.25"),sQuery(id+"F2.wireOp",EDGE,"E43.22.0.25"),sQuery(id+"F2.wireOp",EDGE,"E43.25.0.25"),sQuery(id+"F2.wireOp",EDGE,"E43.28.0.25"),sQuery(id+"F2.wireOp",EDGE,"E43.31.0.25"),sQuery(id+"F2.wireOp",EDGE,"E43.34.0.25"),sQuery(id+"F2.wireOp",EDGE,"E43.37.0.25"),sQuery(id+"F2.wireOp",EDGE,"E43.40.0.25"),sQuery(id+"F2.wireOp",EDGE,"E43.0.0.26"),sQuery(id+"F2.wireOp",EDGE,"E43.3.0.26"),sQuery(id+"F2.wireOp",EDGE,"E43.7.0.26"),sQuery(id+"F2.wireOp",EDGE,"E43.10.0.26"),sQuery(id+"F2.wireOp",EDGE,"E43.13.0.26"),sQuery(id+"F2.wireOp",EDGE,"E43.16.0.26"),sQuery(id+"F2.wireOp",EDGE,"E43.19.0.26"),sQuery(id+"F2.wireOp",EDGE,"E43.22.0.26"),sQuery(id+"F2.wireOp",EDGE,"E43.25.0.26"),sQuery(id+"F2.wireOp",EDGE,"E43.28.0.26"),sQuery(id+"F2.wireOp",EDGE,"E43.31.0.26"),sQuery(id+"F2.wireOp",EDGE,"E43.34.0.26"),sQuery(id+"F2.wireOp",EDGE,"E43.37.0.26"),sQuery(id+"F2.wireOp",EDGE,"E43.40.0.26")])]});
            hole(context, id + "F8", {"style" : HoleStyle.SIMPLE, "endStyle" : HoleEndStyle.THROUGH, "oppositeDirection" : true, "holeDiameter" : 3.78 * mm, "locations" : qUnion([Q0]), "scope" : qUnion([Q1]), "isTappedThrough" : true});
        }
    });
